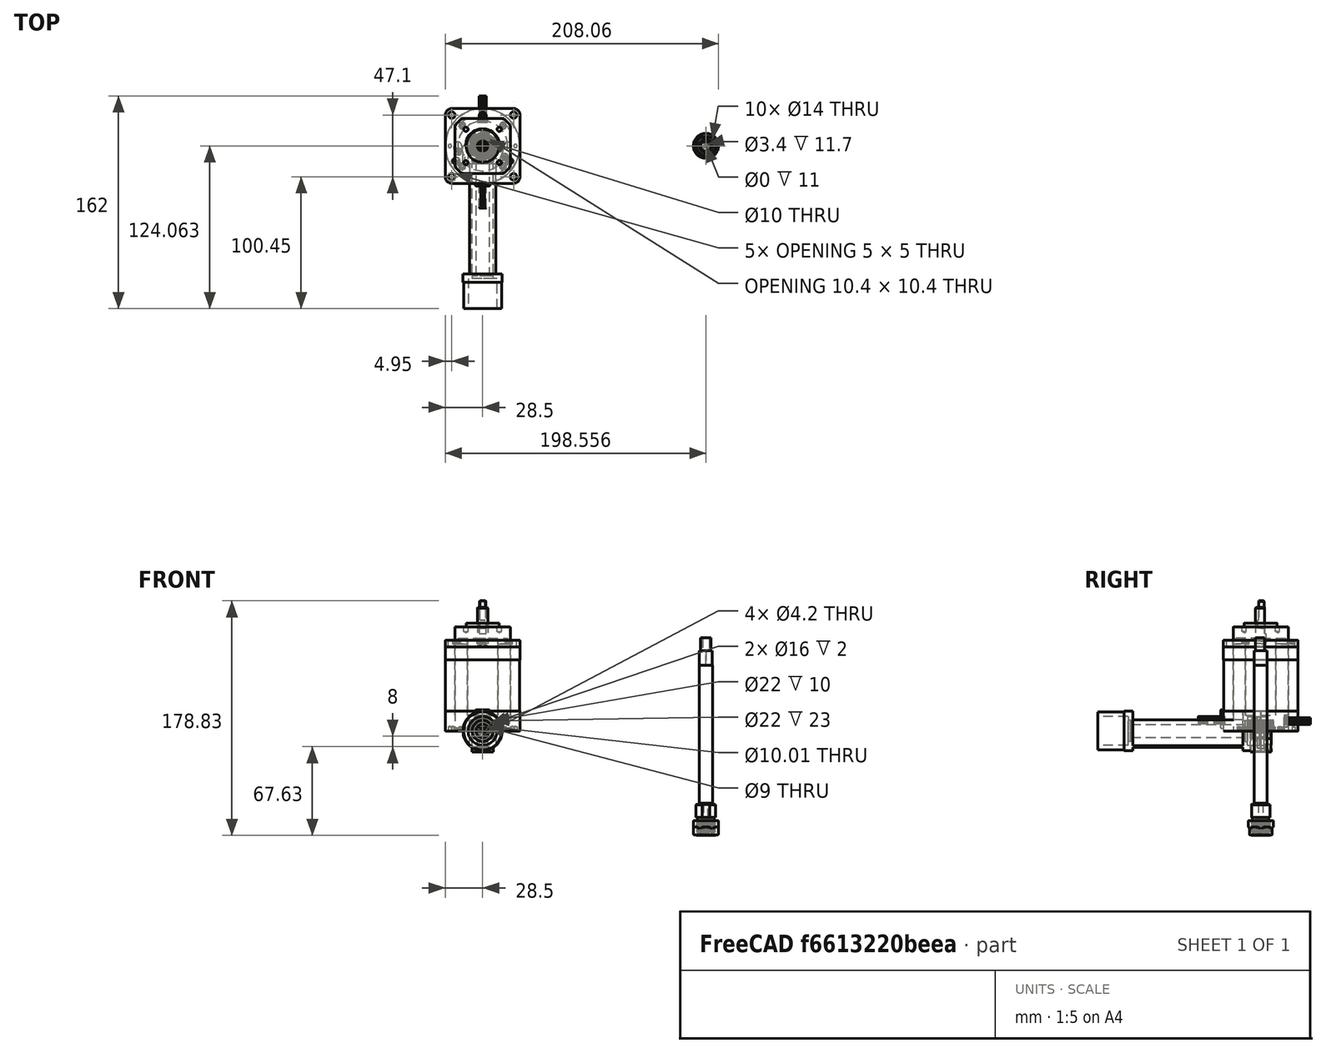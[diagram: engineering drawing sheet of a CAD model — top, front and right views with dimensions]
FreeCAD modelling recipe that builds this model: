
FCSTD DOCUMENT  (FreeCAD 0.21R31155 (Git))
Label: ToolPostDrill
License: All rights reserved
LicenseURL: http://en.wikipedia.org/wiki/All_rights_reserved
objects: TechDraw::DrawViewDimension×42, Sketcher::SketchObject×33, PartDesign::CoordinateSystem×27, PartDesign::Pocket×25, App::Link×18, App::Part×14, PartDesign::Pad×11, PartDesign::Body×10, TechDraw::DrawViewPart×7, Part::Feature×5, PartDesign::Chamfer×5, App::DocumentObjectGroup×4, PartDesign::FeaturePython×4, TechDraw::DrawSVGTemplate×3, TechDraw::DrawPage×3, TechDraw::DrawViewSection×2, PartDesign::ShapeBinder×2, Spreadsheet::Sheet×1, App::FeaturePython×1, PartDesign::Revolution×1
note: 165 computed .brp shape members not serialized (recipe doc carries the construction recipe); baked Part::Feature solids carry a one-line shape summary decoded from their .brp
EXTERNAL_REF file=BLDC Adapter.FCStd obj=MotorFlange
EXTERNAL_REF file=BLDC Adapter.FCStd obj=Part006
EXTERNAL_REF file=BLDC Adapter.FCStd obj=MountingFlange
EXTERNAL_REF file=ToolPost.FCStd obj=Part
EXTERNAL_REF file=ToolPost.FCStd obj=ToolBackRight
EXTERNAL_REF file=ConnectorHousing.FCStd obj=Part
EXTERNAL_REF file=ConnectorHousing.FCStd obj=Back

FEATURE [Spreadsheet::Sheet] Spreadsheet
  Configuration = 2
  cells = A4=Part; B4=HousingDiameter; C4=Length; D4=ToolHeight; E4=ToolHolderHeigth; F4=ShaftPosition; G4=ToolPostLength; H4=ColletShaftBoring; I4=BearingDiameter; J4=BearingWidth; K4=BearingDiameterBase; L4=BearingInnerDiameter; M4=BearingInnerPocketDepth; N4=ShaftDiameter; O4=LockNutThickness; P4=LockNutWasherThickness; Q4=LockNutBoltDiameter; R4=LockNutBoltThreadDiameter; S4=ShaftThreadDiameter; T4=ShaftEndDiameter; U4=ShaftEndLength; V4=ShaftEndDpocketLength; W4=MotorShaftDlength; X4=Wallthickness; Y4=MountingShaftDiameter; Z4=MountingShaftLength; AA4=FrontSpacerWidth; AB4=GearLengthSpindle; AC4=GearHeight; AD4=GearModule; AE4=GearTeeth; AF4=GearHelix; AG4=GearLengthBLDC; AH4=GearShaftPocketDepth; AI4=GearLockBoltThreadDiameter; AJ4=GearLockBoltThreadSeparation; AK4=GearLockBoltPosition; A5==hiddenref(.Configuration.String); B5(HousingDiameter)==.B8; C5(Length)==.C8; D5(ToolHeight)==.D8; E5(ToolHolderHeigth)==.E8; F5(ShaftPosition)==.F8; G5(ToolPostLength)==.G8; H5(ColletShaftBoring)==.H8; I5(BearingDiameter)==.I8; J5(BearingWidth)==.J8; K5(BearingDiameterBase)==.K8; L5(BearingInnerDiameter)==.L8; M5(BearingInnerPocketDepth)==.M8; N5(ShaftDiameter)==.N8; O5(LockNutThickness)==.O8; P5(LockNutWasherThickness)==.P8; Q5(LockNutBoltDiameter)==.Q8; R5(LockNutBoltThreadDiameter)==.R8; S5(ShaftThreadDiameter)==.S8; T5(ShaftEndDiameter)==.T8; U5(ShaftEndLength)==.U8; V5(ShaftEndDpocketLength)==.V8; W5(MotorShaftDlength)==.W8; X5(Wallthickness)==.X8; Y5(MountingShaftDiameter)==.Y8; Z5(MountingShaftLength)==.Z8; AA5(FrontSpacerWidth)==.AA8; AB5(GearLengthSpindle)==.AB8; AC5(GearHeight)==.AC8; AD5(GearModule)==.AD8; AE5(GearTeeth)==.AE8; AF5(GearHelix)==.AF8; AG5(GearLengthBLDC)==.AG8; AH5(GearShaftPocketDepth)==.AH8; AI5(GearLockBoltThreadDiameter)==.AI8; AJ5(GearLockBoltSeparation)==.AJ8; AK5(GearLockBoltPosition)==.AK8; AL5(GearShaftOuterDiameter)==.AL8; A6=BF290 Houder Vertical; B6=29.9; C6=150; D6=12.5; E6=21; F6=10; G6=80; H6=10; I6=22; J6=6; K6=14; L6=18; M6=2; N6=10; O6=5; P6=3; Q6=3; R6=2.5; S6=9.800000000000001; T6=8; U6=10; V6=10; W6=20; X6=3; Y6=28.9; Z6=20; AA6=4; AB6=14; AC6=6; AD6=1.5; AE6=12; AF6=0; AG6=26; AH6=11; AI6=4.2; AJ6=8; AK6=6; AL6=18; A7=DC300 Houder; B7=29.9; C7=150; D7=8.25; E7=14; F7=10; G7=50; H7=10; I7=22; J7=6; K7=14; L7=18; M7=2; N7=10; O7=15; P7=3; Q7=3; R7=2.5; S7=9.800000000000001; T7=8; U7=23; V7=10; W7=17; X7=3; Y7=26; Z7=12; AA7=4; AB7=12; AC7=8; AD7=1.5; AE7=12; AF7=0; AG7=26; AH7=10; AI7=4.2; AJ7=6; AK7=4; AL7=16; A8=BF290 Houder Horizontal; B8=29.9; C8=150; D8=12.5; E8=21; F8=10; G8=80; H8=10; I8=22; J8=6; K8=14; L8=18; M8=2; N8=10; O8=5; P8=3; Q8=3; R8=2.5; S8=9.800000000000001; T8=8; U8=10; V8=10; W8=20; X8=3; Y8=28.9; Z8=20; AA8=4; AB8=14; AC8=8; AD8=1; AE8=18; AF8=0; AG8=24; AH8=11; AI8=4.2; AJ8=8; AK8=4; AL8=16; A12=CalculatedFields; A13=FrontBearingPocketDepth; B13(FrontBearingPocketDepth)==BearingWidth + FrontSpacerWidth; C13=10; A14=BackBearingPocketDepth; B14(BackBearingPocketDepth)==MountingShaftLength + Wallthickness; C14=23; A15=BearingInnerPocketDiameter; B15(BearingInnerPocketDiameter)==(BearingDiameterBase + BearingInnerDiameter) / 2; A16=HousingLength; B16(HousingLength)==FrontBearingPocketDepth + Wallthickness + ToolPostPocketLength + Wallthickness + BackBearingPocketDepth + 1; +40 more cells
  expr: .Configuration.Enum = cells[<<A6:|>>]
  expr: .cells.Bind.B5.ZZ5 = tuple(.cells; <<B>> + str(hiddenref(Configuration) + 6); <<ZZ>> + str(hiddenref(Configuration) + 6))
FEATURE [Sketcher::SketchObject] Sketch
  FullyConstrained = true
  MapMode = 5
  Placement = pos=(0,0,0) rot=(1,0,0;1.5708rad)
  Support = -> [XZ_Plane005]
  expr: Constraints[1] = Spreadsheet.HousingDiameter
  sketch-geometry (1):
    g0: Circle CenterX=0 CenterY=0 CenterZ=0 NormalX=0 NormalY=0 NormalZ=1 AngleXU=0 Radius=14.95
  constraints (2):
    c: Coincident(g0,g-1)
    c: Diameter(g0) = 29.9
FEATURE [PartDesign::Pad] Pad001  label="Housing001"
  Direction = (0,-1,-2e-16)
  Length = 124
  Length2 = 10
  Placement = pos=(0,0,0) rot=(1,0,0;1.5708rad)
  Profile = -> Sketch
  ReferenceAxis = -> Sketch [N_Axis]
  Type = 0
  expr: Length = Spreadsheet.HousingLength
FEATURE [Sketcher::SketchObject] Sketch001
  FullyConstrained = true
  MapMode = 5
  Placement = pos=(0,0,0) rot=(-1,0,0;1.5708rad)
  Support = -> [Pad001]
  expr: Constraints[1] = Spreadsheet.BearingDiameter
  sketch-geometry (1):
    g0: Circle CenterX=0 CenterY=0 CenterZ=0 NormalX=0 NormalY=0 NormalZ=1 AngleXU=0 Radius=11
  constraints (2):
    c: Coincident(g0,g-1)
    c: Diameter(g0) = 22
FEATURE [PartDesign::Pocket] Pocket  label="FrontBearingPocket"
  BaseFeature = -> Pad001
  Direction = (0,-1,-2e-16)
  Length = 10
  Length2 = 5
  Placement = pos=(0,0,0) rot=(1,0,0;1.5708rad)
  Profile = -> Sketch001
  ReferenceAxis = -> Sketch001 [N_Axis]
  Type = 0
  expr: Length = Spreadsheet.FrontBearingPocketDepth
FEATURE [Sketcher::SketchObject] Sketch002
  FullyConstrained = true
  MapMode = 5
  Placement = pos=(0,-10,0) rot=(-1,0,0;1.5708rad)
  Support = -> [Pocket]
  expr: Constraints[1] = Spreadsheet.ShaftBoringDiameter
  sketch-geometry (1):
    g0: Circle CenterX=0 CenterY=0 CenterZ=0 NormalX=0 NormalY=0 NormalZ=1 AngleXU=0 Radius=5.005
  constraints (2):
    c: Coincident(g0,g-1)
    c: Diameter(g0) = 10.01
FEATURE [Sketcher::SketchObject] Sketch004
  AttachmentOffset = pos=(0,0,13.5) rot=(0,0,1;0rad)
  FullyConstrained = true
  MapMode = 5
  Placement = pos=(0,-13.5,-3e-15) rot=(1,0,0;1.5708rad)
  Support = -> [XZ_Plane005]
  expr: .AttachmentOffset.Base.z = Spreadsheet.ToolPostPocketPositionH
  expr: Constraints[13] = Spreadsheet.HousingDiameter + 1
  expr: Constraints[2] = Spreadsheet.ToolHeight
  expr: Constraints[3] = Spreadsheet.HousingDiameter + 1
  expr: Constraints[5] = Spreadsheet.ToolHolderHeigth
  expr: Constraints[7] = Spreadsheet.ShaftPosition
  sketch-geometry (13):
    g0: LineSegment StartX=-9.29289 StartY=-12.5 StartZ=0 EndX=9.29289 EndY=-12.5 EndZ=0
    g1: LineSegment StartX=15.45 StartY=-15.45 StartZ=0 EndX=-15.45 EndY=-15.45 EndZ=0
    g2: LineSegment StartX=-10 StartY=8.5 StartZ=0 EndX=10 EndY=8.5 EndZ=0
    g3: LineSegment StartX=-10 StartY=-11.7929 StartZ=0 EndX=-10 EndY=8.5 EndZ=0
    g4: LineSegment StartX=10 StartY=8.5 StartZ=0 EndX=10 EndY=-11.7929 EndZ=0
    g5: LineSegment StartX=-15.45 StartY=-15.45 StartZ=0 EndX=-15.45 EndY=15.45 EndZ=0
    g6: LineSegment StartX=-15.45 StartY=15.45 StartZ=0 EndX=15.45 EndY=15.45 EndZ=0
    g7: LineSegment StartX=15.45 StartY=15.45 StartZ=0 EndX=15.45 EndY=-15.45 EndZ=0
    g8: GeomPoint X=-15.45 Y=15.45 Z=0
    g9: GeomPoint X=-10 Y=8.5 Z=0
    g10: GeomPoint X=10 Y=8.5 Z=0
    g11: LineSegment StartX=-10 StartY=-11.7929 StartZ=0 EndX=-9.29289 EndY=-12.5 EndZ=0
    g12: LineSegment StartX=10 StartY=-11.7929 StartZ=0 EndX=9.29289 EndY=-12.5 EndZ=0
  constraints (33):
    c: Horizontal(g0)
    c: Symmetric(g1,g1,g-2)
    c: DistanceY(g0,g-1) = 12.5
    c: DistanceX(g1,g1) = 30.9
    c: Symmetric(g9,g10,g-2)
    c: DistanceY(g0,g10) = 21
    c: Vertical(g3)
    c: DistanceX(g-1,g10) = 10
    c: Coincident(g1,g5)
    c: Vertical(g5)
    c: Horizontal(g6)
    c: Coincident(g6,g7)
    c: Coincident(g7,g1)
    c: DistanceY(g7,g7) = 30.9
    c: PointOnObject(g8,g6)
    c: PointOnObject(g8,g5)
    c: Symmetric(g6,g1,g-1)
    c: PointOnObject(g9,g2)
    c: PointOnObject(g9,g3)
    c: PointOnObject(g10,g2)
    c: PointOnObject(g10,g4)
    c: Vertical(g4)
    c: Coincident(g3,g2)
    c: Coincident(g4,g2)
    c: Coincident(g5,g6)
    c: Coincident(g4,g12)
    c: Coincident(g12,g0)
    c: Angle(g12,g0) = 2.35619
    c: Coincident(g3,g11)
    c: Coincident(g11,g0)
    c: Angle(g0,g11) = 2.35619
    c: Distance(g11) = 1
    c: Equal(g11,g12)
FEATURE [Part::Feature] Part__Feature003  label="Body"
  shape: bbox 22 x 6 x 22 mm, 52 faces (baked)
FEATURE [PartDesign::CoordinateSystem] LCS_1  label="Inner"
  AttacherType = Attacher::AttachEngine3D
  MapMode = 11
  Placement = pos=(0,-3,-9e-16) rot=(0.57735,-0.57735,0.57735;2.0944rad)
  Support = -> [Part__Feature003]
FEATURE [PartDesign::CoordinateSystem] LCS_Origin
  AttacherType = Attacher::AttachEngine3D
  MapMode = 2
  Support = -> [X_Axis007]
FEATURE [App::DocumentObjectGroup] Constraints
FEATURE [App::FeaturePython] Variables  # WARN: FeaturePython — macro-defined, semantics opaque (R4)
  Type = App::PropertyContainer
FEATURE [App::DocumentObjectGroup] Configurations
FEATURE [App::Link] Housing  label="Housing002"
  AssemblyType = Part::Link
  AttachedBy = #FrontBearing
  AttachedTo = Parent Assembly#LCS_Origin
  AttachmentOffset = pos=(0,0,72) rot=(0.57735,-0.57735,-0.57735;4.18879rad)
  LinkPlacement = pos=(2.2e-15,10,72) rot=(0,0,1;0rad)
  LinkedObject = -> Part001
  Placement = pos=(2.2e-15,10,72) rot=(0,0,1;0rad)
  SolverId = Asm4EE
  expr: Placement = LCS_Origin.Placement * AttachmentOffset * FrontBearing.Placement ^ -1
FEATURE [App::Link] Bearing002
  AssemblyType = Part::Link
  AttachedBy = #LCS_1
  AttachedTo = Housing#FrontBearing
  AttachmentOffset = pos=(0,0,0) rot=(0,-1,0;3.14159rad)
  LinkPlacement = pos=(1.3e-15,3,72) rot=(0,0,1;0rad)
  LinkedObject = -> Bearing001
  Placement = pos=(1.3e-15,3,72) rot=(0,0,1;0rad)
  SolverId = Asm4EE
  expr: Placement = Housing.Placement * FrontBearing.Placement * AttachmentOffset * LCS_1.Placement ^ -1
FEATURE [App::Link] Bearing003
  AssemblyType = Part::Link
  AttachedBy = #LCS_1
  AttachedTo = Housing#BackBearing
  AttachmentOffset = pos=(0,0,0) rot=(1,0,0;3.14159rad)
  LinkPlacement = pos=(-1.47e-14,-94,72) rot=(0,0,-1;3.14159rad)
  LinkedObject = -> Bearing001
  Placement = pos=(-1.47e-14,-94,72) rot=(0,0,-1;3.14159rad)
  SolverId = Asm4EE
  expr: Placement = Housing.Placement * BackBearing.Placement * AttachmentOffset * LCS_1.Placement ^ -1
FEATURE [PartDesign::CoordinateSystem] Outer
  AttacherType = Attacher::AttachEngine3D
  MapMode = 11
  Placement = pos=(0,3,9e-16) rot=(0.57735,-0.57735,0.57735;2.0944rad)
  Support = -> [Part__Feature003]
FEATURE [App::Part] Bearing001  label="Bearing"
  Group = -> [Part__Feature003,LCS_1,Outer]
  Origin = -> Origin006
FEATURE [Part::Feature] Part__Feature004  label="ER11A_Mutter_Komponente1_einzeln v2"
  Placement = pos=(170.057,0.0630184,-68.3269) rot=(0,1,0;3.14159rad)
  shape: bbox 20.48 x 19.46 x 11.62 mm, 87 faces (baked)
FEATURE [Part::Feature] Part__Feature005  label="Kopf_Aufnahme"
  shape: bbox 15.02 x 14.53 x 22.42 mm, 56 faces (baked)
FEATURE [Sketcher::SketchObject] Sketch011
  FullyConstrained = true
  MapMode = 11
  Placement = pos=(170,-2.2e-15,-55) rot=(0,0,1;1.5708rad)
  Support = -> [Part__Feature005]
  expr: Constraints[1] = Spreadsheet.ShaftDiameter
  sketch-geometry (1):
    g0: Circle CenterX=0 CenterY=0 CenterZ=0 NormalX=0 NormalY=0 NormalZ=1 AngleXU=0 Radius=5
  constraints (2):
    c: Coincident(g0,g-1)
    c: Diameter(g0) = 10
FEATURE [PartDesign::Pad] Pad  label="Shaft"
  Direction = (0,0,1)
  Length = 105
  Length2 = 10
  Profile = -> Sketch011
  ReferenceAxis = -> Sketch011 [N_Axis]
  Type = 0
  expr: Length = Spreadsheet.ShaftLength
FEATURE [Sketcher::SketchObject] Sketch012
  FullyConstrained = false
  MapMode = 11
  Placement = pos=(170,-1.8e-15,50) rot=(0,0,1;3.14159rad)
  Support = -> [Pad]
  expr: Constraints[2] = Spreadsheet.ShaftThreadDiameter
  sketch-geometry (2):
    g0: Circle CenterX=-3.1e-05 CenterY=0 CenterZ=0 NormalX=0 NormalY=0 NormalZ=1 AngleXU=0 Radius=0.00074
    g1: Circle CenterX=-3.1e-05 CenterY=0 CenterZ=0 NormalX=0 NormalY=0 NormalZ=1 AngleXU=0 Radius=4.9
  constraints (3):
    c: PointOnObject(g0,g-1)
    c: Coincident(g1,g0)
    c: Diameter(g1) = 9.8
FEATURE [PartDesign::Pad] Pad004  label="ShaftThread"
  BaseFeature = -> Pad
  Direction = (0,0,1)
  Length = 11
  Length2 = 10
  Profile = -> Sketch012
  ReferenceAxis = -> Sketch012 [N_Axis]
  Type = 0
  expr: Length = Spreadsheet.ShaftThreadLength
FEATURE [Sketcher::SketchObject] Sketch013
  FullyConstrained = true
  MapMode = 11
  Placement = pos=(170,-2e-15,61) rot=(0,0,-1;1.5708rad)
  Support = -> [Pad004]
  expr: Constraints[1] = Spreadsheet.ShaftEndDiameter
  sketch-geometry (1):
    g0: Circle CenterX=0 CenterY=0 CenterZ=0 NormalX=0 NormalY=0 NormalZ=1 AngleXU=0 Radius=4
  constraints (2):
    c: Coincident(g0,g-1)
    c: Diameter(g0) = 8
FEATURE [PartDesign::Pad] Pad005  label="ShaftEnd"
  BaseFeature = -> Pad004
  Direction = (0,0,1)
  Length = 10
  Length2 = 10
  Profile = -> Sketch013
  ReferenceAxis = -> Sketch013 [N_Axis]
  Type = 0
  expr: Length = Spreadsheet.ShaftEndLength
FEATURE [PartDesign::CoordinateSystem] SpindelFrontBearing
  AttacherType = Attacher::AttachEngine3D
  AttachmentOffset = pos=(0,0,-1) rot=(0,0,1;0rad)
  MapMode = 11
  Placement = pos=(170,-2e-15,-56) rot=(0,0,1;3.14159rad)
FEATURE [App::Link] Spindle  label="Spindle001"
  AssemblyType = Part::Link
  AttachedBy = #SpindelFrontBearing
  AttachedTo = SpacerFront#Back002
  AttachmentOffset = pos=(0,0,0) rot=(0,0,-1;3.14159rad)
  LinkPlacement = pos=(2.7e-14,-46,242) rot=(-0.57735,-0.57735,0.57735;4.18879rad)
  LinkedObject = -> Part003
  Placement = pos=(2.7e-14,-46,242) rot=(-0.57735,-0.57735,0.57735;4.18879rad)
  SolverId = Asm4EE
  expr: Placement = SpacerFront.Placement * Back002.Placement * AttachmentOffset * SpindelFrontBearing.Placement ^ -1
FEATURE [Part::Feature] Part__Feature  label="57BLR70-24-02"
  shape: bbox 61.7 x 78.35 x 94.1 mm, 300 faces, 2 solids (baked)
FEATURE [PartDesign::CoordinateSystem] Flange
  AttacherType = Attacher::AttachEngine3D
  MapMode = 11
  Placement = pos=(0,-1.2e-15,69.1) rot=(0,0,-1;1.5708rad)
  Support = -> [Part__Feature]
FEATURE [PartDesign::CoordinateSystem] ShaftTop
  AttacherType = Attacher::AttachEngine3D
  MapMode = 5
  Placement = pos=(0,0,94.1) rot=(0,0,1;0rad)
  Support = -> [Part__Feature]
FEATURE [App::Link] BLDCmotor  label="BLDCmotor001"
  AssemblyType = Part::Link
  AttachedBy = #Flange
  AttachedTo = BLDC_adapter#MotorFlange
  AttachmentOffset = pos=(0,0,0) rot=(1,0,0;3.14159rad)
  LinkPlacement = pos=(-3.42e-14,-209.1,90) rot=(-1,0,0;1.5708rad)
  LinkedObject = -> Part005
  Placement = pos=(-3.42e-14,-209.1,90) rot=(-1,0,0;1.5708rad)
  SolverId = Asm4EE
  expr: Placement = BLDC_adapter.Placement * BLDC_Adapter#MotorFlange.Placement * AttachmentOffset * Flange.Placement ^ -1
FEATURE [Sketcher::SketchObject] Sketch017
  FullyConstrained = true
  MapMode = 5
  Support = -> [XY_Plane019]
  expr: Constraints[2] = Spreadsheet.ShaftDiameter
  expr: Constraints[3] = Spreadsheet.SpacerOuterDiameter
  sketch-geometry (2):
    g0: Circle CenterX=0 CenterY=0 CenterZ=0 NormalX=0 NormalY=0 NormalZ=1 AngleXU=0 Radius=5
    g1: Circle CenterX=0 CenterY=0 CenterZ=0 NormalX=0 NormalY=0 NormalZ=1 AngleXU=0 Radius=10.95
  constraints (4):
    c: Coincident(g0,g-1)
    c: Coincident(g1,g0)
    c: Diameter(g0) = 10
    c: Diameter(g1) = 21.9
FEATURE [PartDesign::Pad] Pad007
  Direction = (0,0,1)
  Length = 4
  Length2 = 10
  Profile = -> Sketch017
  ReferenceAxis = -> Sketch017 [N_Axis]
  Type = 0
  expr: Length = Spreadsheet.FrontSpacerWidth
FEATURE [PartDesign::Chamfer] Chamfer
  Angle = 45
  Base = -> Pad007 [Face4,Face3]
  BaseFeature = -> Pad007
  ChamferType = 0
  FlipDirection = false
  Size = 0.25
  Size2 = 1
  SupportTransform = false
  UseAllEdges = false
FEATURE [PartDesign::CoordinateSystem] Front002
  AttacherType = Attacher::AttachEngine3D
  MapMode = 11
  Placement = pos=(0,0,4) rot=(0,0,1;1.5708rad)
  Support = -> [Chamfer]
FEATURE [PartDesign::CoordinateSystem] Back002
  AttacherType = Attacher::AttachEngine3D
  MapMode = 11
  Placement = pos=(0,0,0) rot=(0,0,1;1.5708rad)
  Support = -> [Chamfer]
FEATURE [App::Link] SpacerFront  label="SpacerFront001"
  AssemblyType = Part::Link
  AttachedBy = #Front002
  AttachedTo = Bearing002#Outer
  AttachmentOffset = pos=(0,0,0) rot=(0,0,-1;3.14159rad)
  LinkPlacement = pos=(3.7e-15,10,72) rot=(0,0.707107,-0.707107;3.14159rad)
  LinkedObject = -> Part006
  Placement = pos=(3.7e-15,10,72) rot=(0,0.707107,-0.707107;3.14159rad)
  SolverId = Asm4EE
  expr: Placement = Bearing002.Placement * Outer.Placement * AttachmentOffset * Front002.Placement ^ -1
FEATURE [App::Link] LockNut001
  AssemblyType = Part::Link
  AttachedBy = #Front003
  AttachedTo = Bearing003#Outer
  AttachmentOffset = pos=(0,0,0) rot=(0,0,-1;3.14159rad)
  LinkPlacement = pos=(-1.42e-14,-102,72) rot=(0,-1,0;4.71239rad)
  LinkedObject = -> LockNut
  Placement = pos=(-1.42e-14,-102,72) rot=(0,-1,0;4.71239rad)
  SolverId = Asm4EE
  expr: Placement = Bearing003.Placement * Outer.Placement * AttachmentOffset * Front003.Placement ^ -1
FEATURE [Sketcher::SketchObject] Sketch019
  FullyConstrained = false
  MapMode = 5
  Placement = pos=(0,0,71) rot=(0,0,1;0rad)
  Support = -> [Pad005]
  expr: Constraints[10] = Spreadsheet.ShaftEndDiameter + 1
  expr: Constraints[9] = Spreadsheet.ShaftDPocketPosition
  sketch-geometry (5):
    g0: LineSegment StartX=165.948 StartY=5 StartZ=0 EndX=174.948 EndY=5 EndZ=0
    g1: LineSegment StartX=174.948 StartY=5 StartZ=0 EndX=174.948 EndY=3 EndZ=0
    g2: LineSegment StartX=174.948 StartY=3 StartZ=0 EndX=165.948 EndY=3 EndZ=0
    g3: LineSegment StartX=165.948 StartY=3 StartZ=0 EndX=165.948 EndY=5 EndZ=0
    g4: GeomPoint X=170.529 Y=0 Z=0
  constraints (12):
    c: Coincident(g0,g1)
    c: Coincident(g1,g2)
    c: Coincident(g2,g3)
    c: Coincident(g3,g0)
    c: Horizontal(g0)
    c: Horizontal(g2)
    c: Vertical(g1)
    c: Vertical(g3)
    c: PointOnObject(g4,g-1)
    c: DistanceY(g4,g1) = 3
    c: DistanceX(g0,g0) = 9
    c: DistanceY(g1,g1) = 2
FEATURE [PartDesign::Pocket] Pocket006
  BaseFeature = -> Pad005
  Direction = (0,0,-1)
  Length = 10
  Length2 = 5
  Profile = -> Sketch019
  ReferenceAxis = -> Sketch019 [N_Axis]
  Type = 0
  expr: Length = Spreadsheet.ShaftEndDpocketLength
FEATURE [PartDesign::Body] Body  label="Body004"
  Group = -> [Sketch011,Pad,Sketch012,Pad004,Sketch013,Pad005,Sketch019,Pocket006]
  Origin = -> Origin014
  Tip = -> Pocket006
FEATURE [PartDesign::CoordinateSystem] Back004
  AttacherType = Attacher::AttachEngine3D
  MapMode = 11
  Placement = pos=(170,-1.8e-15,71) rot=(0,0,1;0rad)
  Support = -> [Pocket006]
FEATURE [TechDraw::DrawSVGTemplate] Template
  EditableTexts = Designed_by_Name=Huub Buis; Drawing_number=Drawing number; FC-Date=20221216; FC-SC=Scale; FC-SH=Sheet; FC-Title=BF290 Drill holder - ER11; Subtitle=V01; Weight=Weight
  Height = 210
  Orientation = 1
  Template = C:/Program Files/FreeCAD 0.19/data/Mod/TechDraw/Templates/A4_LandscapeTD.svg
  Width = 297
FEATURE [Sketcher::SketchObject] Sketch021
  FullyConstrained = true
  MapMode = 5
  Placement = pos=(0,-10,0) rot=(-1,0,0;1.5708rad)
  Support = -> [Pocket]
  expr: Constraints[1] = Spreadsheet.BearingInnerPocketDiameter
  sketch-geometry (1):
    g0: Circle CenterX=0 CenterY=0 CenterZ=0 NormalX=0 NormalY=0 NormalZ=1 AngleXU=0 Radius=8
  constraints (2):
    c: Coincident(g0,g-1)
    c: Diameter(g0) = 16
FEATURE [PartDesign::Pocket] Pocket007  label="FrontBearingInnerPocket"
  BaseFeature = -> Pocket
  Direction = (0,-1,-2e-16)
  Length = 2
  Length2 = 5
  Placement = pos=(0,0,0) rot=(1,0,0;1.5708rad)
  Profile = -> Sketch021
  ReferenceAxis = -> Sketch021 [N_Axis]
  Type = 0
  expr: Length = Spreadsheet.BearingInnerPocketDepth
FEATURE [PartDesign::Pocket] Pocket001  label="ShaftPocket"
  BaseFeature = -> Pocket007
  Direction = (0,-1,-2e-16)
  Length = 5
  Length2 = 5
  Placement = pos=(0,0,0) rot=(1,0,0;1.5708rad)
  Profile = -> Sketch002
  ReferenceAxis = -> Sketch002 [N_Axis]
  Type = 1
FEATURE [Sketcher::SketchObject] Sketch003
  FullyConstrained = true
  MapMode = 5
  Placement = pos=(0,-124,3e-16) rot=(1,0,0;1.5708rad)
  Support = -> [Pocket001]
  expr: Constraints[1] = Spreadsheet.BearingDiameter
  sketch-geometry (1):
    g0: Circle CenterX=0 CenterY=0 CenterZ=0 NormalX=0 NormalY=0 NormalZ=1 AngleXU=0 Radius=11
  constraints (2):
    c: Coincident(g0,g-1)
    c: Diameter(g0) = 22
FEATURE [PartDesign::Pocket] Pocket002  label="BackBearingPocket"
  BaseFeature = -> Pocket001
  Direction = (0,1,2e-16)
  Length = 23
  Length2 = 5
  Placement = pos=(0,0,0) rot=(1,0,0;1.5708rad)
  Profile = -> Sketch003
  ReferenceAxis = -> Sketch003 [N_Axis]
  Type = 0
  expr: Length = Spreadsheet.BackBearingPocketDepth
FEATURE [Sketcher::SketchObject] Sketch022
  FullyConstrained = true
  MapMode = 5
  Placement = pos=(0,-101,2.24e-14) rot=(1,0,0;1.5708rad)
  Support = -> [Pocket002]
  expr: Constraints[1] = Spreadsheet.BearingInnerPocketDiameter
  sketch-geometry (1):
    g0: Circle CenterX=0 CenterY=0 CenterZ=0 NormalX=0 NormalY=0 NormalZ=1 AngleXU=0 Radius=8
  constraints (2):
    c: Coincident(g0,g-1)
    c: Diameter(g0) = 16
FEATURE [PartDesign::Pocket] Pocket008  label="BackBearingInnerPocket"
  BaseFeature = -> Pocket002
  Direction = (0,1,-2e-16)
  Length = 2
  Length2 = 5
  Placement = pos=(0,0,0) rot=(1,0,0;1.5708rad)
  Profile = -> Sketch022
  ReferenceAxis = -> Sketch022 [N_Axis]
  Type = 0
  expr: Length = Spreadsheet.BearingInnerPocketDepth
FEATURE [PartDesign::Pocket] Pocket003  label="ToolPostPocket"
  BaseFeature = -> Pocket008
  Direction = (0,1,2e-16)
  Length = 84
  Length2 = 5
  Placement = pos=(0,0,0) rot=(1,0,0;1.5708rad)
  Profile = -> Sketch004
  ReferenceAxis = -> Sketch004 [N_Axis]
  Reversed = true
  Type = 0
  expr: Length = Spreadsheet.ToolPostPocketLength
FEATURE [PartDesign::CoordinateSystem] BackBearing
  AttacherType = Attacher::AttachEngine3D
  MapMode = 11
  Placement = pos=(0,-101,-5.6e-15) rot=(0.57735,-0.57735,0.57735;2.0944rad)
  Support = -> [Pocket003]
FEATURE [PartDesign::CoordinateSystem] FrontBearing
  AttacherType = Attacher::AttachEngine3D
  MapMode = 11
  Placement = pos=(0,-10,2.2e-15) rot=(0.57735,-0.57735,-0.57735;4.18879rad)
  Support = -> [Pocket003]
FEATURE [Sketcher::SketchObject] Sketch015
  FullyConstrained = true
  MapMode = 5
  Placement = pos=(0,-124,3e-16) rot=(1,0,0;1.5708rad)
  Support = -> [Pocket003]
  expr: Constraints[1] = Spreadsheet.MountingShaftDiameter
  expr: Constraints[3] = Spreadsheet.HousingDiameter + 1
  sketch-geometry (2):
    g0: Circle CenterX=0 CenterY=0 CenterZ=0 NormalX=0 NormalY=0 NormalZ=1 AngleXU=0 Radius=14.45
    g1: Circle CenterX=0 CenterY=0 CenterZ=0 NormalX=0 NormalY=0 NormalZ=1 AngleXU=0 Radius=15.45
  constraints (4):
    c: Coincident(g0,g-1)
    c: Diameter(g0) = 28.9
    c: Coincident(g1,g0)
    c: Diameter(g1) = 30.9
FEATURE [PartDesign::Pocket] Pocket005  label="MountingShaftPocket"
  BaseFeature = -> Pocket003
  Direction = (0,1,2e-16)
  Length = 20
  Length2 = 5
  Placement = pos=(0,0,0) rot=(1,0,0;1.5708rad)
  Profile = -> Sketch015
  ReferenceAxis = -> Sketch015 [N_Axis]
  Type = 0
  expr: Length = Spreadsheet.MountingShaftLength
FEATURE [PartDesign::Body] Body001  label="HousingBody"
  Group = -> [Sketch,Pad001,Sketch001,Pocket,Pocket007,Sketch002,Pocket001,Sketch003,Pocket002,Pocket008,Sketch004,Pocket003,Sketch015,Pocket005,Sketch021,Sketch022]
  Origin = -> Origin005
  Tip = -> Pocket005
FEATURE [PartDesign::CoordinateSystem] MountingShaft001  label="MountingShaft002"
  AttacherType = Attacher::AttachEngine3D
  MapMode = 11
  Placement = pos=(0,-124,-5e-16) rot=(0.57735,-0.57735,0.57735;2.0944rad)
  Support = -> [Pocket005]
FEATURE [App::Part] Part001  label="Housing"
  Group = -> [Body001,BackBearing,FrontBearing,MountingShaft001]
  Origin = -> Origin004
FEATURE [TechDraw::DrawViewPart] View  label="Housing003"
  CoarseView = false
  Direction = (1,0,0)
  Focus = 100
  HardHidden = true
  IsoCount = 0
  IsoHidden = false
  IsoVisible = false
  LockPosition = false
  Perspective = false
  Rotation = 0
  ScaleType = 0
  SeamHidden = false
  SeamVisible = false
  SmoothHidden = false
  SmoothVisible = true
  Source = -> [Part001]
  X = 89.0384
  XDirection = (0,1,0)
  Y = 160.956
FEATURE [TechDraw::DrawViewSection] SectionView  label="Section A - A"
  BaseView = -> View
  CoarseView = false
  CutSurfaceDisplay = 2
  Direction = (0,1e-16,-1)
  FileGeomPattern = C:/Program Files/FreeCAD 0.19/data/Mod/TechDraw/PAT/FCPAT.pat
  FileHatchPattern = C:/Program Files/FreeCAD 0.19/data/Mod/TechDraw/Patterns/simple.svg
  Focus = 100
  FuseBeforeCut = false
  HardHidden = false
  HatchScale = 1
  IsoCount = 0
  IsoHidden = false
  IsoVisible = false
  LockPosition = false
  NameGeomPattern = Diamant
  Perspective = false
  Rotation = 0
  ScaleType = 0
  SeamHidden = false
  SeamVisible = true
  SectionDirection = 4
  SectionNormal = (0,1e-16,-1)
  SectionOrigin = (0,-61.99,0.033)
  SectionSymbol = A
  SmoothHidden = false
  SmoothVisible = true
  Source = -> [Part001]
  TrimAfterCut = false
  X = 135.319
  XDirection = (0,1,1e-16)
  Y = 101.209
FEATURE [TechDraw::DrawViewDimension] Dimension010
  AngleOverride = false
  Arbitrary = false
  ArbitraryTolerances = false
  EqualTolerance = true
  ExtensionAngle = 0
  FormatSpec = %.2f
  FormatSpecOverTolerance = %+.2f
  FormatSpecUnderTolerance = %+.2f
  Inverted = false
  LineAngle = 0
  LockPosition = false
  MeasureType = 1
  OverTolerance = 0
  References2D = -> [SectionView]
  Rotation = 0
  ScaleType = 0
  TheoreticalExact = false
  Type = 1
  UnderTolerance = 0
  X = -55.4134
  Y = -34.9784
FEATURE [TechDraw::DrawSVGTemplate] Template001
  EditableTexts = Designed_by_Name=Designed by Name; Drawing_number=Drawing number; FC-Date=Date; FC-SC=Scale; FC-SH=Sheet; FC-Title=Title; Subtitle=Subtitle; Weight=Weight
  Height = 210
  Orientation = 1
  Template = C:/Program Files/FreeCAD 0.19/data/Mod/TechDraw/Templates/A4_LandscapeTD.svg
  Width = 297
FEATURE [Sketcher::SketchObject] Sketch023
  FullyConstrained = true
  MapMode = 5
  Placement = pos=(0,0,4) rot=(0,0,1;0rad)
  Support = -> [Pad007]
  expr: Constraints[2] = Spreadsheet.BearingInnerPocketDiameter
  expr: Constraints[3] = Spreadsheet.SpacerOuterDiameter
  sketch-geometry (2):
    g0: Circle CenterX=0 CenterY=0 CenterZ=0 NormalX=0 NormalY=0 NormalZ=1 AngleXU=0 Radius=8
    g1: Circle CenterX=0 CenterY=0 CenterZ=0 NormalX=0 NormalY=0 NormalZ=1 AngleXU=0 Radius=10.95
  constraints (4):
    c: Coincident(g0,g-1)
    c: Coincident(g1,g0)
    c: Diameter(g0) = 16
    c: Diameter(g1) = 21.9
FEATURE [PartDesign::Pocket] Pocket009
  BaseFeature = -> Chamfer
  Direction = (0,0,-1)
  Length = 1
  Length2 = 5
  Profile = -> Sketch023
  ReferenceAxis = -> Sketch023 [N_Axis]
  Type = 0
FEATURE [PartDesign::Body] Body005  label="Body006"
  Group = -> [Sketch017,Pad007,Chamfer,Sketch023,Pocket009]
  Origin = -> Origin019
  Tip = -> Pocket009
FEATURE [App::Part] Part006  label="SpacerFront"
  Group = -> [Body005,Front002,Back002]
  Origin = -> Origin018
FEATURE [TechDraw::DrawViewPart] View004  label="Spacer FV"
  CoarseView = false
  Direction = (0,-1,0)
  Focus = 100
  HardHidden = false
  IsoCount = 0
  IsoHidden = false
  IsoVisible = false
  LockPosition = false
  Perspective = false
  Rotation = 0
  ScaleType = 0
  SeamHidden = false
  SeamVisible = true
  SmoothHidden = false
  SmoothVisible = true
  Source = -> [Part006]
  X = 32.6631
  XDirection = (1,0,0)
  Y = 163.585
FEATURE [TechDraw::DrawViewDimension] Dimension016
  AngleOverride = false
  Arbitrary = false
  ArbitraryTolerances = false
  EqualTolerance = true
  ExtensionAngle = 0
  FormatSpec = %.2f
  FormatSpecOverTolerance = %+.2f
  FormatSpecUnderTolerance = %+.2f
  Inverted = false
  LineAngle = 0
  LockPosition = false
  MeasureType = 1
  OverTolerance = 0
  References2D = -> [View004]
  Rotation = 0
  ScaleType = 0
  TheoreticalExact = false
  Type = 2
  UnderTolerance = 0
  X = 18.1775
  Y = 27.7079
FEATURE [TechDraw::DrawViewDimension] Dimension017
  AngleOverride = false
  Arbitrary = false
  ArbitraryTolerances = false
  EqualTolerance = true
  ExtensionAngle = 0
  FormatSpec = %.2f
  FormatSpecOverTolerance = %+.2f
  FormatSpecUnderTolerance = %+.2f
  Inverted = false
  LineAngle = 0
  LockPosition = false
  MeasureType = 1
  OverTolerance = 0
  References2D = -> [View004]
  Rotation = 0
  ScaleType = 0
  TheoreticalExact = false
  Type = 2
  UnderTolerance = 0
  X = 27.9886
  Y = 28.1012
FEATURE [TechDraw::DrawViewSection] SectionView001  label="Section A - A001"
  BaseView = -> View004
  CoarseView = false
  CutSurfaceDisplay = 2
  Direction = (1,0,0)
  FileGeomPattern = C:/Program Files/FreeCAD 0.19/data/Mod/TechDraw/PAT/FCPAT.pat
  FileHatchPattern = C:/Program Files/FreeCAD 0.19/data/Mod/TechDraw/Patterns/simple.svg
  Focus = 100
  FuseBeforeCut = false
  HardHidden = false
  HatchScale = 1
  IsoCount = 0
  IsoHidden = false
  IsoVisible = false
  LockPosition = false
  NameGeomPattern = Diamant
  Perspective = false
  Rotation = 0
  ScaleType = 0
  SeamHidden = false
  SeamVisible = true
  SectionDirection = 4
  SectionNormal = (1,0,0)
  SectionOrigin = (0.02,0,2)
  SectionSymbol = A
  SmoothHidden = false
  SmoothVisible = true
  Source = -> [Part006]
  TrimAfterCut = false
  X = 104.982
  XDirection = (0,0,1)
  Y = 166.774
FEATURE [TechDraw::DrawViewDimension] Dimension021
  AngleOverride = false
  Arbitrary = false
  ArbitraryTolerances = false
  EqualTolerance = true
  ExtensionAngle = 0
  FormatSpec = %.2f
  FormatSpecOverTolerance = %+.2f
  FormatSpecUnderTolerance = %+.2f
  Inverted = false
  LineAngle = 0
  LockPosition = false
  MeasureType = 1
  OverTolerance = 0
  References2D = -> [SectionView001]
  Rotation = 0
  ScaleType = 0
  TheoreticalExact = false
  Type = 2
  UnderTolerance = 0
  X = 9.95315
  Y = 1.13586
FEATURE [TechDraw::DrawViewDimension] Dimension022
  AngleOverride = false
  Arbitrary = false
  ArbitraryTolerances = false
  EqualTolerance = true
  ExtensionAngle = 0
  FormatSpec = %.2f
  FormatSpecOverTolerance = %+.2f
  FormatSpecUnderTolerance = %+.2f
  Inverted = false
  LineAngle = 0
  LockPosition = false
  MeasureType = 1
  OverTolerance = 0
  References2D = -> [SectionView001]
  Rotation = 0
  ScaleType = 0
  TheoreticalExact = false
  Type = 2
  UnderTolerance = 0
  X = 17.7375
  Y = 1.77002
FEATURE [TechDraw::DrawViewDimension] Dimension023
  AngleOverride = false
  Arbitrary = false
  ArbitraryTolerances = false
  EqualTolerance = true
  ExtensionAngle = 0
  FormatSpec = %.2f
  FormatSpecOverTolerance = %+.2f
  FormatSpecUnderTolerance = %+.2f
  Inverted = false
  LineAngle = 0
  LockPosition = false
  MeasureType = 1
  OverTolerance = 0
  References2D = -> [SectionView001]
  Rotation = 0
  ScaleType = 0
  TheoreticalExact = false
  Type = 2
  UnderTolerance = 0
  X = 26.9666
  Y = 2.34357
FEATURE [TechDraw::DrawViewDimension] Dimension024
  AngleOverride = false
  Arbitrary = false
  ArbitraryTolerances = false
  EqualTolerance = true
  ExtensionAngle = 0
  FormatSpec = %.2f
  FormatSpecOverTolerance = %+.2f
  FormatSpecUnderTolerance = %+.2f
  Inverted = false
  LineAngle = 0
  LockPosition = false
  MeasureType = 1
  OverTolerance = 0
  References2D = -> [SectionView]
  Rotation = 0
  ScaleType = 0
  TheoreticalExact = false
  Type = 2
  UnderTolerance = 0
  X = -70.9878
  Y = 2.35719
FEATURE [TechDraw::DrawViewDimension] Dimension025
  AngleOverride = false
  Arbitrary = false
  ArbitraryTolerances = false
  EqualTolerance = true
  ExtensionAngle = 0
  FormatSpec = %.2f
  FormatSpecOverTolerance = %+.2f
  FormatSpecUnderTolerance = %+.2f
  Inverted = false
  LineAngle = 0
  LockPosition = false
  MeasureType = 1
  OverTolerance = 0
  References2D = -> [SectionView]
  Rotation = 0
  ScaleType = 0
  TheoreticalExact = false
  Type = 2
  UnderTolerance = 0
  X = -86.2687
  Y = 2.07158
FEATURE [TechDraw::DrawViewDimension] Dimension026
  AngleOverride = false
  Arbitrary = false
  ArbitraryTolerances = false
  EqualTolerance = true
  ExtensionAngle = 0
  FormatSpec = %.2f
  FormatSpecOverTolerance = %+.2f
  FormatSpecUnderTolerance = %+.2f
  Inverted = false
  LineAngle = 0
  LockPosition = false
  MeasureType = 1
  OverTolerance = 0
  References2D = -> [SectionView]
  Rotation = 0
  ScaleType = 0
  TheoreticalExact = false
  Type = 2
  UnderTolerance = 0
  X = -97.273
  Y = 3.64245
FEATURE [TechDraw::DrawViewDimension] Dimension027
  AngleOverride = false
  Arbitrary = false
  ArbitraryTolerances = false
  EqualTolerance = true
  ExtensionAngle = 0
  FormatSpec = %.2f
  FormatSpecOverTolerance = %+.2f
  FormatSpecUnderTolerance = %+.2f
  Inverted = false
  LineAngle = 0
  LockPosition = false
  MeasureType = 1
  OverTolerance = 0
  References2D = -> [SectionView]
  Rotation = 0
  ScaleType = 0
  TheoreticalExact = false
  Type = 2
  UnderTolerance = 0
  X = -105.127
  Y = 3.78525
FEATURE [TechDraw::DrawViewDimension] Dimension029
  AngleOverride = false
  Arbitrary = false
  ArbitraryTolerances = false
  EqualTolerance = true
  ExtensionAngle = 0
  FormatSpec = %.2f
  FormatSpecOverTolerance = %+.2f
  FormatSpecUnderTolerance = %+.2f
  Inverted = false
  LineAngle = 0
  LockPosition = false
  MeasureType = 1
  OverTolerance = 0
  References2D = -> [SectionView]
  Rotation = 0
  ScaleType = 0
  TheoreticalExact = false
  Type = 1
  UnderTolerance = 0
  X = 81.9719
  Y = 3.92927
FEATURE [TechDraw::DrawViewDimension] Dimension032
  AngleOverride = false
  Arbitrary = false
  ArbitraryTolerances = false
  EqualTolerance = true
  ExtensionAngle = 0
  FormatSpec = %.2f
  FormatSpecOverTolerance = %+.2f
  FormatSpecUnderTolerance = %+.2f
  Inverted = false
  LineAngle = 0
  LockPosition = false
  MeasureType = 1
  OverTolerance = 0
  References2D = -> [SectionView]
  Rotation = 0
  ScaleType = 0
  TheoreticalExact = false
  Type = 1
  UnderTolerance = 0
  X = 81.9308
  Y = 13.2358
FEATURE [TechDraw::DrawSVGTemplate] Template002
  EditableTexts = Designed_by_Name=Designed by Name; Drawing_number=Drawing number; FC-Date=Date; FC-SC=Scale; FC-SH=Sheet; FC-Title=Title; Subtitle=Subtitle; Weight=Weight
  Height = 210
  Orientation = 1
  Template = C:/Program Files/FreeCAD 0.19/data/Mod/TechDraw/Templates/A4_LandscapeTD.svg
  Width = 297
FEATURE [Sketcher::SketchObject] Sketch024
  FullyConstrained = true
  MapMode = 5
  Placement = pos=(0,0,0) rot=(0.57735,0.57735,0.57735;2.0944rad)
  Support = -> [YZ_Plane025]
  expr: Constraints[13] = Spreadsheet.LockNutThreadDiameter / 2
  expr: Constraints[14] = Spreadsheet.LockNutDiameter / 2
  expr: Constraints[15] = Spreadsheet.BearingDiameterBase / 2
  expr: Constraints[17] = Spreadsheet.LockNutThickness
  sketch-geometry (6):
    g0: LineSegment StartX=0 StartY=10.9 StartZ=0 EndX=4.5 EndY=10.9 EndZ=0
    g1: LineSegment StartX=4.5 StartY=10.9 StartZ=0 EndX=4.5 EndY=7 EndZ=0
    g2: LineSegment StartX=4.5 StartY=7 StartZ=0 EndX=5 EndY=7 EndZ=0
    g3: LineSegment StartX=5 StartY=7 StartZ=0 EndX=5 EndY=4.5 EndZ=0
    g4: LineSegment StartX=5 StartY=4.5 StartZ=0 EndX=0 EndY=4.5 EndZ=0
    g5: LineSegment StartX=0 StartY=4.5 StartZ=0 EndX=0 EndY=10.9 EndZ=0
  constraints (18):
    c: PointOnObject(g0,g-2)
    c: Horizontal(g0)
    c: Coincident(g0,g1)
    c: Vertical(g1)
    c: Coincident(g1,g2)
    c: Horizontal(g2)
    c: Coincident(g2,g3)
    c: Vertical(g3)
    c: Coincident(g3,g4)
    c: PointOnObject(g4,g-2)
    c: Horizontal(g4)
    c: Coincident(g4,g5)
    c: Coincident(g5,g0)
    c: DistanceY(g-1,g4) = 4.5
    c: DistanceY(g-1,g0) = 10.9
    c: DistanceY(g-1,g2) = 7
    c: DistanceX(g2,g2) = 0.5
    c: DistanceX(g4,g4) = 5
FEATURE [PartDesign::Revolution] Revolution
  Angle = 360
  Axis = (1e-16,1,-1e-16)
  Base = (0,0,0)
  Placement = pos=(0,0,0) rot=(0.57735,0.57735,0.57735;2.0944rad)
  Profile = -> Sketch024
  ReferenceAxis = -> Y_Axis025
FEATURE [Sketcher::SketchObject] Sketch025
  FullyConstrained = true
  MapMode = 5
  Placement = pos=(0,-5e-16,0) rot=(0.57735,0.57735,-0.57735;2.0944rad)
  Support = -> [Revolution]
  expr: Constraints[2] = Spreadsheet.LockNutBoltSeparation
  expr: Constraints[3] = Spreadsheet.LockNutBoltDiameter
  sketch-geometry (2):
    g0: Circle CenterX=0 CenterY=8 CenterZ=0 NormalX=0 NormalY=0 NormalZ=1 AngleXU=0 Radius=1.5
    g1: Circle CenterX=0 CenterY=-8 CenterZ=0 NormalX=0 NormalY=0 NormalZ=1 AngleXU=0 Radius=1.5
  constraints (5):
    c: PointOnObject(g0,g-2)
    c: Symmetric(g0,g1,g-1)
    c: DistanceY(g1,g0) = 16
    c: Diameter(g0) = 3
    c: Equal(g0,g1)
FEATURE [PartDesign::Pocket] Pocket010
  BaseFeature = -> Revolution
  Direction = (2e-16,1,-4e-16)
  Length = 5
  Length2 = 5
  Placement = pos=(0,0,0) rot=(0.57735,0.57735,0.57735;2.0944rad)
  Profile = -> Sketch025
  ReferenceAxis = -> Sketch025 [N_Axis]
  Type = 1
FEATURE [PartDesign::Body] Body007  label="LockNutNut"
  Group = -> [Sketch024,Revolution,Sketch025,Pocket010]
  Origin = -> Origin025
  Tip = -> Pocket010
FEATURE [Sketcher::SketchObject] Sketch026
  FullyConstrained = true
  MapMode = 5
  Placement = pos=(0,0,0) rot=(1,0,0;1.5708rad)
  Support = -> [XZ_Plane026]
  expr: Constraints[2] = Spreadsheet.LockNutThreadDiameter
  expr: Constraints[3] = Spreadsheet.LockNutBoltThreadDiameter
  expr: Constraints[5] = Spreadsheet.LockNutDiameter
  expr: Constraints[7] = Spreadsheet.LockNutBoltSeparation
  sketch-geometry (4):
    g0: Circle CenterX=0 CenterY=0 CenterZ=0 NormalX=0 NormalY=0 NormalZ=1 AngleXU=0 Radius=4.5
    g1: Circle CenterX=0 CenterY=0 CenterZ=0 NormalX=0 NormalY=0 NormalZ=1 AngleXU=0 Radius=10.9
    g2: Circle CenterX=-8 CenterY=0 CenterZ=0 NormalX=0 NormalY=0 NormalZ=1 AngleXU=0 Radius=1.25
    g3: Circle CenterX=8 CenterY=0 CenterZ=0 NormalX=0 NormalY=0 NormalZ=1 AngleXU=0 Radius=1.25
  constraints (9):
    c: Coincident(g0,g-1)
    c: Coincident(g1,g0)
    c: Diameter(g0) = 9
    c: Diameter(g2) = 2.5
    c: Equal(g2,g3)
    c: Diameter(g1) = 21.8
    c: Symmetric(g3,g2,g0)
    c: Distance(g2,g3) = 16
    c: PointOnObject(g2,g-1)
FEATURE [PartDesign::Pad] Pad009
  Direction = (0,-1,-2e-16)
  Length = 3
  Length2 = 10
  Placement = pos=(0,0,0) rot=(1,0,0;1.5708rad)
  Profile = -> Sketch026
  ReferenceAxis = -> Sketch026 [N_Axis]
  Type = 0
  expr: Length = Spreadsheet.LockNutWasherThickness
FEATURE [PartDesign::CoordinateSystem] Back
  AttacherType = Attacher::AttachEngine3D
  MapMode = 11
  Placement = pos=(0,-3,7e-16) rot=(0.57735,-0.57735,0.57735;2.0944rad)
  Support = -> [Pad009]
FEATURE [PartDesign::Body] Body008  label="LockNutDisk"
  Group = -> [Sketch026,Pad009,Back]
  Origin = -> Origin026
  Placement = pos=(0,-1,0) rot=(0,0,1;0rad)
  Tip = -> Pad009
FEATURE [PartDesign::CoordinateSystem] Front003
  AttacherType = Attacher::AttachEngine3D
  MapMode = 11
  Placement = pos=(6e-16,5,-1.8e-15) rot=(-1,0,0;1.5708rad)
  Support = -> [Pocket010]
FEATURE [App::Part] LockNut
  Group = -> [Body007,Body008,Front003]
  Origin = -> Origin022
FEATURE [PartDesign::CoordinateSystem] ThreadStart
  AttacherType = Attacher::AttachEngine3D
  MapMode = 11
  Placement = pos=(170,-1.8e-15,50) rot=(0,0,1;3.14159rad)
  Support = -> [Pocket006]
FEATURE [PartDesign::CoordinateSystem] EndStart
  AttacherType = Attacher::AttachEngine3D
  MapMode = 11
  Placement = pos=(170,-2e-15,61) rot=(0,0,-1;1.5708rad)
  Support = -> [Pocket006]
FEATURE [App::Part] ER11_Spindle_8x100mm_v2  label="ER11 Spindle_8x100mm v2"
  Group = -> [Part__Feature004,Part__Feature005,Body,EndStart]
  Origin = -> Origin
FEATURE [App::Part] Part003  label="Spindle"
  Group = -> [ER11_Spindle_8x100mm_v2,SpindelFrontBearing,Back004,ThreadStart]
  Origin = -> Origin013
FEATURE [TechDraw::DrawViewPart] View006  label="Part"
  CoarseView = false
  Direction = (0.851,0.429,0.303)
  Focus = 100
  HardHidden = false
  IsoCount = 0
  IsoHidden = false
  IsoVisible = false
  LockPosition = false
  Perspective = false
  Rotation = 0
  ScaleType = 0
  SeamHidden = false
  SeamVisible = true
  SmoothHidden = false
  SmoothVisible = true
  Source = -> [Part003]
  X = 211.81
  XDirection = (-0.45,0.295,0.843)
  Y = 155.608
FEATURE [TechDraw::DrawViewPart] View007  label="FV"
  CoarseView = false
  Direction = (1,0,0)
  Focus = 100
  HardHidden = false
  IsoCount = 0
  IsoHidden = false
  IsoVisible = false
  LockPosition = false
  Perspective = false
  Rotation = 270
  ScaleType = 0
  SeamHidden = false
  SeamVisible = true
  SmoothHidden = false
  SmoothVisible = true
  Source = -> [Part003]
  X = 84.063
  XDirection = (0,1,0)
  Y = 81.1692
FEATURE [TechDraw::DrawViewDimension] Dimension036
  AngleOverride = false
  Arbitrary = false
  ArbitraryTolerances = false
  EqualTolerance = true
  ExtensionAngle = 0
  FormatSpec = %.2f
  FormatSpecOverTolerance = %+.2f
  FormatSpecUnderTolerance = %+.2f
  Inverted = false
  LineAngle = 0
  LockPosition = false
  MeasureType = 1
  OverTolerance = 0
  References2D = -> [View007]
  Rotation = 0
  ScaleType = 0
  TheoreticalExact = false
  Type = 1
  UnderTolerance = 0
  X = 89.3849
  Y = 22.8891
FEATURE [TechDraw::DrawViewDimension] Dimension039
  AngleOverride = false
  Arbitrary = true
  ArbitraryTolerances = false
  EqualTolerance = true
  ExtensionAngle = 0
  FormatSpec = M10x1
  FormatSpecOverTolerance = %+.2f
  FormatSpecUnderTolerance = %+.2f
  Inverted = false
  LineAngle = 0
  LockPosition = false
  MeasureType = 1
  OverTolerance = 0
  References2D = -> [View007]
  Rotation = 0
  ScaleType = 0
  TheoreticalExact = false
  Type = 2
  UnderTolerance = 0
  X = 84.0724
  Y = -7.58136
FEATURE [TechDraw::DrawViewDimension] Dimension035
  AngleOverride = false
  Arbitrary = false
  ArbitraryTolerances = false
  EqualTolerance = true
  ExtensionAngle = 0
  FormatSpec = %.2f
  FormatSpecOverTolerance = %+.2f
  FormatSpecUnderTolerance = %+.2f
  Inverted = false
  LineAngle = 0
  LockPosition = false
  MeasureType = 1
  OverTolerance = 0
  References2D = -> [View007]
  Rotation = 0
  ScaleType = 0
  TheoreticalExact = false
  Type = 1
  UnderTolerance = 0
  X = 43.1486
  Y = 22.9128
FEATURE [TechDraw::DrawViewDimension] Dimension034
  AngleOverride = false
  Arbitrary = false
  ArbitraryTolerances = false
  EqualTolerance = true
  ExtensionAngle = 0
  FormatSpec = %.2f
  FormatSpecOverTolerance = %+.2f
  FormatSpecUnderTolerance = %+.2f
  Inverted = false
  LineAngle = 0
  LockPosition = false
  MeasureType = 1
  OverTolerance = 0
  References2D = -> [View007]
  Rotation = 0
  ScaleType = 0
  TheoreticalExact = false
  Type = 1
  UnderTolerance = 0
  X = 2.07988
  Y = 18.9234
FEATURE [TechDraw::DrawViewDimension] Dimension038
  AngleOverride = false
  Arbitrary = true
  ArbitraryTolerances = false
  EqualTolerance = true
  ExtensionAngle = 0
  FormatSpec = 8 mm D=7
  FormatSpecOverTolerance = %+.2f
  FormatSpecUnderTolerance = %+.2f
  Inverted = false
  LineAngle = 0
  LockPosition = false
  MeasureType = 1
  OverTolerance = 0
  References2D = -> [View007]
  Rotation = 0
  ScaleType = 0
  TheoreticalExact = false
  Type = 2
  UnderTolerance = 0
  X = 107.08
  Y = 1.78744
FEATURE [TechDraw::DrawViewDimension] Dimension050
  AngleOverride = false
  Arbitrary = false
  ArbitraryTolerances = false
  EqualTolerance = true
  ExtensionAngle = 0
  FormatSpec = %.2f
  FormatSpecOverTolerance = %+.2f
  FormatSpecUnderTolerance = %+.2f
  Inverted = false
  LineAngle = 0
  LockPosition = false
  MeasureType = 1
  OverTolerance = 0
  References2D = -> [View007]
  Rotation = 0
  ScaleType = 0
  TheoreticalExact = false
  Type = 1
  UnderTolerance = 0
  X = 5.62656
  Y = -22.4269
FEATURE [TechDraw::DrawPage] Page002  label="Spindle002"
  KeepUpdated = true
  NextBalloonIndex = 1
  ProjectionType = 0
  Template = -> Template002
  Views = -> [View006,View007,Dimension034,Dimension035,Dimension036,Dimension038,Dimension039,Dimension050]
FEATURE [App::Link] Link  label="BLDC adapter"
  LinkedObject = -> <external BLDC Adapter.FCStd>#Part006
FEATURE [App::Link] BLDC_adapter  label="BLDC adapter001"
  AssemblyType = Part::Link
  AttachedBy = #MountingFlange
  AttachedTo = Housing#BackBearing
  AttachmentOffset = pos=(0,0,6) rot=(0,0,1;0rad)
  LinkPlacement = pos=(-2.69e-14,-136,90) rot=(-1,0,0;4.71239rad)
  LinkedObject = -> <external BLDC Adapter.FCStd>#Part006
  Placement = pos=(-2.69e-14,-136,90) rot=(-1,0,0;4.71239rad)
  SolverId = Asm4EE
  expr: Placement = Housing.Placement * BackBearing.Placement * AttachmentOffset * BLDC_Adapter#MountingFlange.Placement ^ -1
FEATURE [TechDraw::DrawViewDimension] Dimension051
  AngleOverride = false
  Arbitrary = false
  ArbitraryTolerances = false
  EqualTolerance = true
  ExtensionAngle = 0
  FormatSpec = %.2f
  FormatSpecOverTolerance = %+.2f
  FormatSpecUnderTolerance = %+.2f
  Inverted = false
  LineAngle = 0
  LockPosition = false
  MeasureType = 1
  OverTolerance = 0
  References2D = -> [SectionView]
  Rotation = 0
  ScaleType = 0
  TheoreticalExact = false
  Type = 1
  UnderTolerance = 0
  X = -49.9996
  Y = -20.3399
FEATURE [TechDraw::DrawViewDimension] Dimension052
  AngleOverride = false
  Arbitrary = false
  ArbitraryTolerances = false
  EqualTolerance = true
  ExtensionAngle = 0
  FormatSpec = %.2f
  FormatSpecOverTolerance = %+.2f
  FormatSpecUnderTolerance = %+.2f
  Inverted = false
  LineAngle = 0
  LockPosition = false
  MeasureType = 1
  OverTolerance = 0
  References2D = -> [SectionView]
  Rotation = 0
  ScaleType = 0
  TheoreticalExact = false
  Type = 1
  UnderTolerance = 0
  X = 58.3662
  Y = -30.6408
FEATURE [TechDraw::DrawViewDimension] Dimension053
  AngleOverride = false
  Arbitrary = false
  ArbitraryTolerances = false
  EqualTolerance = true
  ExtensionAngle = 0
  FormatSpec = %.2f
  FormatSpecOverTolerance = %+.2f
  FormatSpecUnderTolerance = %+.2f
  Inverted = false
  LineAngle = 0
  LockPosition = false
  MeasureType = 1
  OverTolerance = 0
  References2D = -> [View]
  Rotation = 0
  ScaleType = 0
  TheoreticalExact = false
  Type = 2
  UnderTolerance = 0
  X = -10.9965
  Y = 2.46336
FEATURE [TechDraw::DrawViewDimension] Dimension054
  AngleOverride = false
  Arbitrary = false
  ArbitraryTolerances = false
  EqualTolerance = true
  ExtensionAngle = 0
  FormatSpec = %.2f
  FormatSpecOverTolerance = %+.2f
  FormatSpecUnderTolerance = %+.2f
  Inverted = false
  LineAngle = 0
  LockPosition = false
  MeasureType = 1
  OverTolerance = 0
  References2D = -> [View]
  Rotation = 0
  ScaleType = 0
  TheoreticalExact = false
  Type = 2
  UnderTolerance = 0
  X = -27.025
  Y = -0.912105
FEATURE [TechDraw::DrawViewDimension] Dimension055
  AngleOverride = false
  Arbitrary = false
  ArbitraryTolerances = false
  EqualTolerance = true
  ExtensionAngle = 0
  FormatSpec = %.2f
  FormatSpecOverTolerance = %+.2f
  FormatSpecUnderTolerance = %+.2f
  Inverted = false
  LineAngle = 0
  LockPosition = false
  MeasureType = 1
  OverTolerance = 0
  References2D = -> [View]
  Rotation = 0
  ScaleType = 0
  TheoreticalExact = false
  Type = 2
  UnderTolerance = 0
  X = 35.803
  Y = 20.2875
FEATURE [TechDraw::DrawViewDimension] Dimension056
  AngleOverride = false
  Arbitrary = false
  ArbitraryTolerances = false
  EqualTolerance = true
  ExtensionAngle = 0
  FormatSpec = %.2f
  FormatSpecOverTolerance = %+.2f
  FormatSpecUnderTolerance = %+.2f
  Inverted = false
  LineAngle = 0
  LockPosition = false
  MeasureType = 1
  OverTolerance = 0
  References2D = -> [View]
  Rotation = 0
  ScaleType = 0
  TheoreticalExact = false
  Type = 2
  UnderTolerance = 0
  X = 10.413
  Y = 2.27836
FEATURE [TechDraw::DrawViewPart] View010  label="FV001"
  CoarseView = false
  Direction = (0,1,0)
  Focus = 100
  HardHidden = true
  IsoCount = 0
  IsoHidden = false
  IsoVisible = false
  LockPosition = false
  Perspective = false
  Rotation = 0
  ScaleType = 0
  SeamHidden = false
  SeamVisible = true
  SmoothHidden = false
  SmoothVisible = true
  Source = -> [Part001]
  X = 208.178
  XDirection = (-1,0,0)
  Y = 162.049
FEATURE [TechDraw::DrawViewDimension] Dimension059
  AngleOverride = false
  Arbitrary = false
  ArbitraryTolerances = false
  EqualTolerance = true
  ExtensionAngle = 0
  FormatSpec = %.2f
  FormatSpecOverTolerance = %+.2f
  FormatSpecUnderTolerance = %+.2f
  Inverted = false
  LineAngle = 0
  LockPosition = false
  MeasureType = 1
  OverTolerance = 0
  References2D = -> [SectionView]
  Rotation = 0
  ScaleType = 0
  TheoreticalExact = false
  Type = 2
  UnderTolerance = 0
  X = 33.7046
  Y = 18.1312
FEATURE [TechDraw::DrawViewDimension] Dimension060
  AngleOverride = false
  Arbitrary = false
  ArbitraryTolerances = false
  EqualTolerance = true
  ExtensionAngle = 0
  FormatSpec = %.2f
  FormatSpecOverTolerance = %+.2f
  FormatSpecUnderTolerance = %+.2f
  Inverted = false
  LineAngle = 0
  LockPosition = false
  MeasureType = 1
  OverTolerance = 0
  References2D = -> [SectionView]
  Rotation = 0
  ScaleType = 0
  TheoreticalExact = false
  Type = 2
  UnderTolerance = 0
  X = 33.6277
  Y = -15.1838
FEATURE [TechDraw::DrawViewDimension] Dimension061
  AngleOverride = false
  Arbitrary = false
  ArbitraryTolerances = false
  EqualTolerance = true
  ExtensionAngle = 0
  FormatSpec = %.2f
  FormatSpecOverTolerance = %+.2f
  FormatSpecUnderTolerance = %+.2f
  Inverted = false
  LineAngle = 0
  LockPosition = false
  MeasureType = 1
  OverTolerance = 0
  References2D = -> [SectionView]
  Rotation = 0
  ScaleType = 0
  TheoreticalExact = false
  Type = 2
  UnderTolerance = 0
  X = -117.234
  Y = 4.08804
FEATURE [TechDraw::DrawViewDimension] Dimension062
  AngleOverride = false
  Arbitrary = false
  ArbitraryTolerances = false
  EqualTolerance = true
  ExtensionAngle = 0
  FormatSpec = %.2f
  FormatSpecOverTolerance = %+.2f
  FormatSpecUnderTolerance = %+.2f
  Inverted = false
  LineAngle = 0
  LockPosition = false
  MeasureType = 1
  OverTolerance = 0
  References2D = -> [SectionView]
  Rotation = 0
  ScaleType = 0
  TheoreticalExact = false
  Type = 1
  UnderTolerance = 0
  X = 6.3015
  Y = 23.8148
FEATURE [TechDraw::DrawViewDimension] Dimension063
  AngleOverride = false
  Arbitrary = false
  ArbitraryTolerances = false
  EqualTolerance = true
  ExtensionAngle = 0
  FormatSpec = %.2f
  FormatSpecOverTolerance = %+.2f
  FormatSpecUnderTolerance = %+.2f
  Inverted = false
  LineAngle = 0
  LockPosition = false
  MeasureType = 1
  OverTolerance = 0
  References2D = -> [View]
  Rotation = 0
  ScaleType = 0
  TheoreticalExact = false
  Type = 1
  UnderTolerance = 0
  X = -4.07398
  Y = 31.0599
FEATURE [TechDraw::DrawViewDimension] Dimension
  AngleOverride = false
  Arbitrary = false
  ArbitraryTolerances = false
  EqualTolerance = true
  ExtensionAngle = 0
  FormatSpec = %.2f
  FormatSpecOverTolerance = %+.2f
  FormatSpecUnderTolerance = %+.2f
  Inverted = false
  LineAngle = 0
  LockPosition = false
  MeasureType = 1
  OverTolerance = 0
  References2D = -> [View]
  Rotation = 0
  ScaleType = 0
  TheoreticalExact = false
  Type = 1
  UnderTolerance = 0
  X = -3.94092
  Y = 38.0271
FEATURE [TechDraw::DrawViewDimension] Dimension064
  AngleOverride = false
  Arbitrary = false
  ArbitraryTolerances = false
  EqualTolerance = true
  ExtensionAngle = 0
  FormatSpec = %.2f
  FormatSpecOverTolerance = %+.2f
  FormatSpecUnderTolerance = %+.2f
  Inverted = false
  LineAngle = 0
  LockPosition = false
  MeasureType = 1
  OverTolerance = 0
  References2D = -> [View]
  Rotation = 0
  ScaleType = 0
  TheoreticalExact = false
  Type = 1
  UnderTolerance = 0
  X = -48.4879
  Y = 23.5819
FEATURE [TechDraw::DrawViewDimension] Dimension065
  AngleOverride = false
  Arbitrary = false
  ArbitraryTolerances = false
  EqualTolerance = true
  ExtensionAngle = 0
  FormatSpec = %.2f
  FormatSpecOverTolerance = %+.2f
  FormatSpecUnderTolerance = %+.2f
  Inverted = false
  LineAngle = 0
  LockPosition = false
  MeasureType = 1
  OverTolerance = 0
  References2D = -> [View]
  Rotation = 0
  ScaleType = 0
  TheoreticalExact = false
  Type = 2
  UnderTolerance = 0
  X = 24.2358
  Y = 4.16273
FEATURE [TechDraw::DrawPage] Page  label="HousingDrawing"
  KeepUpdated = true
  NextBalloonIndex = 1
  ProjectionType = 0
  Template = -> Template
  Views = -> [View,SectionView,Dimension010,Dimension024,Dimension025,Dimension026,Dimension027,Dimension029,Dimension032,Dimension051,Dimension052,Dimension053,Dimension054,Dimension055,Dimension056,View010,Dimension059,Dimension060,Dimension061,Dimension062,Dimension063,Dimension,Dimension064,Dimension065]
FEATURE [Sketcher::SketchObject] Sketch031
  FullyConstrained = true
  MapMode = 5
  Support = -> [XY_Plane032]
  expr: Constraints[1] = Spreadsheet.GearShaftOuterDiameter
  sketch-geometry (1):
    g0: Circle CenterX=0 CenterY=0 CenterZ=0 NormalX=0 NormalY=0 NormalZ=1 AngleXU=0 Radius=8
  constraints (2):
    c: Coincident(g0,g-1)
    c: Diameter(g0) = 16
FEATURE [PartDesign::Pad] Pad012
  Direction = (0,0,1)
  Length = 6
  Length2 = 10
  Profile = -> Sketch031
  ReferenceAxis = -> Sketch031 [N_Axis]
  Reversed = true
  Type = 0
  expr: Length = Spreadsheet.GearLengthSpindle - Spreadsheet.GearHeight
FEATURE [Sketcher::SketchObject] Sketch032
  AttachmentOffset = pos=(0,0,-6) rot=(0,0,1;0rad)
  FullyConstrained = true
  MapMode = 5
  Placement = pos=(0,0,-6) rot=(0,0,1;0rad)
  Support = -> [XY_Plane032]
  expr: .AttachmentOffset.Base.z = -Spreadsheet.GearShaftLength
  expr: Constraints[4] = Spreadsheet.ShaftCouplerInnerDiameter
  expr: Constraints[5] = Spreadsheet.ShaftCouplerInnerDiameter / 2 - 1
  sketch-geometry (2):
    g0: ArcOfCircle CenterX=0 CenterY=0 CenterZ=0 NormalX=0 NormalY=0 NormalZ=1 AngleXU=0 Radius=4.075 StartAngle=2.28655 EndAngle=7.13823
    g1: LineSegment StartX=-2.67395 StartY=3.075 StartZ=0 EndX=2.67395 EndY=3.075 EndZ=0
  constraints (6):
    c: Coincident(g0,g-1)
    c: Horizontal(g1)
    c: Coincident(g0,g1)
    c: Coincident(g0,g1)
    c: Diameter(g0) = 8.15
    c: DistanceY(g0,g0) = 3.075
FEATURE [PartDesign::Pocket] Pocket011  label="ShaftPocket001"
  BaseFeature = -> Pad012
  Direction = (0,0,-1)
  Length = 11
  Length2 = 5
  Profile = -> Sketch032
  ReferenceAxis = -> Sketch032 [N_Axis]
  Reversed = true
  Type = 1
  expr: Length = Spreadsheet.GearShaftPocketDepth
FEATURE [App::Link] BevelGearSpindle  label="BevelGearSpindle001"
  AssemblyType = Part::Link
  AttachedBy = #Gear
  AttachedTo = Spindle#Back004
  LinkPlacement = pos=(-3.3e-14,-117,72) rot=(0,-0.707107,0.707107;3.14159rad)
  LinkedObject = -> Part009
  Placement = pos=(-3.3e-14,-117,72) rot=(0,-0.707107,0.707107;3.14159rad)
  SolverId = Asm4EE
  expr: Placement = Spindle.Placement * Back004.Placement * AttachmentOffset * Gear.Placement ^ -1
FEATURE [PartDesign::Chamfer] Chamfer002  label="Chamferhaft"
  Angle = 45
  Base = -> Pocket011 [Edge6,Edge7]
  BaseFeature = -> Pocket011
  ChamferType = 0
  FlipDirection = false
  Size = 0.3
  Size2 = 1
  SupportTransform = false
  UseAllEdges = false
FEATURE [PartDesign::FeaturePython] BevelGear002  # WARN: FeaturePython — macro-defined, semantics opaque (R4)
  AttacherType = Attacher::AttachEngine3D
  BaseFeature = -> Chamfer002
  angular_backlash = 0
  backlash = 0
  beta = 0
  clearance = 0.1
  dw = 18
  height = 8
  module = 1
  numpoints = 6
  pitch_angle = 45
  pressure_angle = 20
  reset_origin = true
  teeth = 18
  version = 0.0.4
  expr: angular_backlash = backlash / dw * 360° / pi
  expr: beta = Spreadsheet.GearHelix
  expr: dw = teeth * module
  expr: height = Spreadsheet.GearHeight
  expr: module = Spreadsheet.GearModule
  expr: teeth = Spreadsheet.GearTeeth
FEATURE [PartDesign::CoordinateSystem] Back005
  AttacherType = Attacher::AttachEngine3D
  MapMode = 11
  Placement = pos=(0,0,-6) rot=(0,0,1;1.5708rad)
  Support = -> [Chamfer002]
FEATURE [Sketcher::SketchObject] Sketch033
  FullyConstrained = true
  MapMode = 5
  Support = -> [XY_Plane034]
  expr: Constraints[1] = Spreadsheet.GearShaftOuterDiameter
  sketch-geometry (1):
    g0: Circle CenterX=0 CenterY=0 CenterZ=0 NormalX=0 NormalY=0 NormalZ=1 AngleXU=0 Radius=8
  constraints (2):
    c: Coincident(g0,g-1)
    c: Diameter(g0) = 16
FEATURE [PartDesign::Pad] Pad013
  Direction = (0,0,1)
  Length = 16
  Length2 = 10
  Profile = -> Sketch033
  ReferenceAxis = -> Sketch033 [N_Axis]
  Reversed = true
  Type = 0
  expr: Length = Spreadsheet.GearLengthBLDC - Spreadsheet.GearHeight
FEATURE [App::Link] BevelGearBLDC  label="BevelGearBLDC001"
  AssemblyType = Part::Link
  AttachedBy = #Gear003
  AttachedTo = BLDCmotor#ShaftTop
  AttachmentOffset = pos=(0,0,0) rot=(0,0,-1;3.14159rad)
  LinkPlacement = pos=(-2.68e-14,-115,90) rot=(0.57735,-0.57735,-0.57735;4.18879rad)
  LinkedObject = -> Part010
  Placement = pos=(-2.68e-14,-115,90) rot=(0.57735,-0.57735,-0.57735;4.18879rad)
  SolverId = Asm4EE
  expr: Placement = BLDCmotor.Placement * ShaftTop.Placement * AttachmentOffset * Gear003.Placement ^ -1
FEATURE [Sketcher::SketchObject] Sketch035
  FullyConstrained = true
  MapMode = 5
  Support = -> [XY_Plane032]
  expr: Constraints[1] = Spreadsheet.GearTeethPocketDiameter
  expr: Constraints[3] = Spreadsheet.GearTeethPocketDiameter * 2
  sketch-geometry (2):
    g0: Circle CenterX=0 CenterY=0 CenterZ=0 NormalX=0 NormalY=0 NormalZ=1 AngleXU=0 Radius=9
    g1: Circle CenterX=0 CenterY=0 CenterZ=0 NormalX=0 NormalY=0 NormalZ=1 AngleXU=0 Radius=18
  constraints (4):
    c: Coincident(g0,g-1)
    c: Diameter(g0) = 18
    c: Coincident(g1,g0)
    c: Diameter(g1) = 36
FEATURE [PartDesign::Pocket] Pocket015  label="TeethPocket001"
  BaseFeature = -> BevelGear002
  Direction = (0,0,-1)
  Length = 5
  Length2 = 5
  Profile = -> Sketch035
  ReferenceAxis = -> Sketch035 [N_Axis]
  Reversed = true
  Type = 1
FEATURE [PartDesign::CoordinateSystem] Back006
  AttacherType = Attacher::AttachEngine3D
  MapMode = 11
  Placement = pos=(0,0,0) rot=(0,0,1;3.73186rad)
  Support = -> [Pocket015]
FEATURE [Sketcher::SketchObject] Sketch036
  FullyConstrained = true
  MapMode = 5
  Support = -> [XY_Plane034]
  expr: Constraints[2] = Spreadsheet.GearTeethPocketDiameter * 2
  expr: Constraints[3] = Spreadsheet.GearTeethPocketDiameter
  sketch-geometry (2):
    g0: Circle CenterX=0 CenterY=0 CenterZ=0 NormalX=0 NormalY=0 NormalZ=1 AngleXU=0 Radius=18
    g1: Circle CenterX=0 CenterY=0 CenterZ=0 NormalX=0 NormalY=0 NormalZ=1 AngleXU=0 Radius=9
  constraints (4):
    c: Coincident(g0,g-1)
    c: Coincident(g1,g0)
    c: Diameter(g0) = 36
    c: Diameter(g1) = 18
FEATURE [PartDesign::CoordinateSystem] Gear
  AttacherType = Attacher::AttachEngine3D
  MapMode = 11
  Placement = pos=(0,0,0) rot=(0,0,1;1.5708rad)
  Support = -> [Pad012]
FEATURE [Sketcher::SketchObject] Sketch034
  FullyConstrained = true
  MapMode = 5
  Support = -> [XY_Plane034]
  expr: Constraints[4] = Spreadsheet.ShaftCouplerInnerDiameter
  expr: Constraints[5] = Spreadsheet.ShaftCouplerInnerDiameter / 2 - 1
  sketch-geometry (2):
    g0: ArcOfCircle CenterX=0 CenterY=0 CenterZ=0 NormalX=0 NormalY=0 NormalZ=1 AngleXU=0 Radius=4.075 StartAngle=2.28655 EndAngle=7.13823
    g1: LineSegment StartX=-2.67395 StartY=3.075 StartZ=0 EndX=2.67395 EndY=3.075 EndZ=0
  constraints (6):
    c: Coincident(g0,g-1)
    c: Horizontal(g1)
    c: Coincident(g0,g1)
    c: Coincident(g0,g1)
    c: Diameter(g0) = 8.15
    c: DistanceY(g0,g0) = 3.075
FEATURE [PartDesign::Pocket] Pocket013  label="ShaftPocket002"
  BaseFeature = -> Pad013
  Direction = (0,0,-1)
  Length = 11
  Length2 = 5
  Profile = -> Sketch034
  ReferenceAxis = -> Sketch034 [N_Axis]
  Type = 1
  expr: Length = Spreadsheet.GearShaftPocketDepth
FEATURE [PartDesign::Chamfer] Chamfer003  label="ShaftChamfer"
  Angle = 45
  Base = -> Pocket013 [Edge6,Edge7]
  BaseFeature = -> Pocket013
  ChamferType = 0
  FlipDirection = false
  Size = 0.3
  Size2 = 1
  SupportTransform = false
  UseAllEdges = false
FEATURE [PartDesign::FeaturePython] BevelGear003  # WARN: FeaturePython — macro-defined, semantics opaque (R4)
  AttacherType = Attacher::AttachEngine3D
  BaseFeature = -> Chamfer003
  angular_backlash = 0
  backlash = 0
  beta = 0
  clearance = 0.1
  dw = 18
  height = 8
  module = 1
  numpoints = 6
  pitch_angle = 45
  pressure_angle = 20
  reset_origin = true
  teeth = 18
  version = 0.0.4
  expr: angular_backlash = backlash / dw * 360° / pi
  expr: beta = Spreadsheet.GearHelix
  expr: dw = teeth * module
  expr: height = Spreadsheet.GearHeight
  expr: module = Spreadsheet.GearModule
  expr: teeth = Spreadsheet.GearTeeth
FEATURE [PartDesign::Pocket] Pocket016  label="TeethPocket"
  BaseFeature = -> BevelGear003
  Direction = (0,0,-1)
  Length = 5
  Length2 = 5
  Profile = -> Sketch036
  ReferenceAxis = -> Sketch036 [N_Axis]
  Reversed = true
  Type = 1
FEATURE [PartDesign::CoordinateSystem] Gear003
  AttacherType = Attacher::AttachEngine3D
  MapMode = 11
  Placement = pos=(0,0,0) rot=(0,0,1;1.5708rad)
  Support = -> [Chamfer003]
FEATURE [PartDesign::Pocket] Pocket017  label="GearShaftPocket"
  BaseFeature = -> Pocket016
  Direction = (0,0,-1)
  Length = 5
  Length2 = 5
  Profile = -> Pocket016 [Face35]
  Type = 1
FEATURE [Sketcher::SketchObject] Sketch037
  AttachmentOffset = pos=(0,0,-9) rot=(0,0,1;0rad)
  FullyConstrained = true
  MapMode = 5
  Placement = pos=(0,9,2e-15) rot=(1,0,0;1.5708rad)
  Support = -> [XZ_Plane034]
  expr: .AttachmentOffset.Base.z = -Spreadsheet.GearTeethPocketDiameter / 2
  expr: Constraints[2] = Spreadsheet.GearLockBoltThreadDiameter
  expr: Constraints[4] = Spreadsheet.GearLockBoltSeparation
  expr: Constraints[5] = Spreadsheet.GearLockBoltPosition
  sketch-geometry (2):
    g0: Circle CenterX=0 CenterY=-4 CenterZ=0 NormalX=0 NormalY=0 NormalZ=1 AngleXU=0 Radius=2.1
    g1: Circle CenterX=0 CenterY=-12 CenterZ=0 NormalX=0 NormalY=0 NormalZ=1 AngleXU=0 Radius=2.1
  constraints (6):
    c: PointOnObject(g0,g-2)
    c: PointOnObject(g1,g-2)
    c: Diameter(g0) = 4.2
    c: Equal(g0,g1)
    c: DistanceY(g1,g0) = 8
    c: DistanceY(g0,g-1) = 4
FEATURE [PartDesign::Pocket] Pocket018  label="LockBoltPocket021"
  BaseFeature = -> Pocket017
  Direction = (0,1,2e-16)
  Length = 9
  Length2 = 5
  Profile = -> Sketch037
  ReferenceAxis = -> Sketch037 [N_Axis]
  Reversed = true
  Type = 0
  expr: Length = Spreadsheet.GearTeethPocketDiameter / 2
FEATURE [PartDesign::Body] Body012
  Group = -> [Sketch033,Pad013,Sketch034,Pocket013,Chamfer003,BevelGear003,Sketch036,Pocket016,Pocket017,Sketch037,Pocket018]
  Origin = -> Origin034
  Tip = -> Pocket018
FEATURE [App::Part] Part010  label="BevelGearBLDC"
  Group = -> [Body012,Back006,Gear003]
  Origin = -> Origin033
FEATURE [PartDesign::Pocket] Pocket019  label="GearPocket"
  BaseFeature = -> Pocket015
  Direction = (0,0,-1)
  Length = 5
  Length2 = 5
  Profile = -> Pocket015 [Face35]
  Type = 1
FEATURE [Sketcher::SketchObject] Sketch038  label="LockBoltPocket"
  AttachmentOffset = pos=(0,0,-8) rot=(0,0,1;0rad)
  FullyConstrained = true
  MapMode = 5
  Placement = pos=(0,8,1.8e-15) rot=(1,0,0;1.5708rad)
  Support = -> [XZ_Plane032]
  expr: .AttachmentOffset.Base.z = -Spreadsheet.GearShaftOuterDiameter / 2
  expr: Constraints[1] = Spreadsheet.GearLockBoltThreadDiameter
  expr: Constraints[2] = Spreadsheet.GearShaftLength / 2
  sketch-geometry (1):
    g0: Circle CenterX=0 CenterY=-3 CenterZ=0 NormalX=0 NormalY=0 NormalZ=1 AngleXU=0 Radius=2.1
  constraints (3):
    c: PointOnObject(g0,g-2)
    c: Diameter(g0) = 4.2
    c: DistanceY(g0,g-1) = 3
FEATURE [PartDesign::Pocket] Pocket020  label="LockBoltPocket020"
  BaseFeature = -> Pocket019
  Direction = (0,1,2e-16)
  Length = 8
  Length2 = 5
  Profile = -> Sketch038
  ReferenceAxis = -> Sketch038 [N_Axis]
  Reversed = true
  Type = 0
  expr: Length = Spreadsheet.GearShaftOuterDiameter / 2
FEATURE [PartDesign::Body] Body011
  Group = -> [Sketch031,Pad012,Sketch032,Pocket011,Chamfer002,BevelGear002,Sketch035,Pocket015,Pocket019,Sketch038,Pocket020]
  Origin = -> Origin032
  Placement = pos=(0,0,0) rot=(0,0,1;0.139626rad)
  Tip = -> Pocket020
FEATURE [App::Part] Part009  label="BevelGearSpindle"
  Group = -> [Body011,Back005,Gear]
  Origin = -> Origin031
FEATURE [App::Link] Link001  label="TopSlide"
  LinkedObject = -> <external ToolPost.FCStd>#Part
FEATURE [App::Link] TopSlide  label="TopSlide001"
  AssemblyType = Part::Link
  AttachedBy = #ToolBackRight
  AttachedTo = Housing#BackBearing
  AttachmentOffset = pos=(-12.5,10,-4) rot=(-0.57735,-0.57735,-0.57735;2.0944rad)
  LinkPlacement = pos=(-34,-7,20.75) rot=(0,0,1;4.71239rad)
  LinkedObject = -> <external ToolPost.FCStd>#Part
  Placement = pos=(-34,-7,20.75) rot=(0,0,1;4.71239rad)
  SolverId = Asm4EE
  expr: Placement = Housing.Placement * BackBearing.Placement * AttachmentOffset * ToolPost#ToolBackRight.Placement ^ -1
FEATURE [Sketcher::SketchObject] Sketch039
  FullyConstrained = true
  MapMode = 5
  Support = -> [XY_Plane036]
  expr: Constraints[1] = Spreadsheet.GearShaftOuterDiameter
  sketch-geometry (1):
    g0: Circle CenterX=0 CenterY=0 CenterZ=0 NormalX=0 NormalY=0 NormalZ=1 AngleXU=0 Radius=8
  constraints (2):
    c: Coincident(g0,g-1)
    c: Diameter(g0) = 16
FEATURE [PartDesign::Pad] Pad014
  Direction = (0,0,1)
  Length = 6
  Length2 = 10
  Profile = -> Sketch039
  ReferenceAxis = -> Sketch039 [N_Axis]
  Reversed = true
  Type = 0
  expr: Length = Spreadsheet.GearLengthSpindle - Spreadsheet.GearHeight
FEATURE [Sketcher::SketchObject] Sketch040
  AttachmentOffset = pos=(0,0,-6) rot=(0,0,1;0rad)
  FullyConstrained = true
  MapMode = 5
  Placement = pos=(0,0,-6) rot=(0,0,1;0rad)
  Support = -> [XY_Plane036]
  expr: .AttachmentOffset.Base.z = -Spreadsheet.GearShaftLength
  expr: Constraints[4] = Spreadsheet.ShaftCouplerInnerDiameter
  expr: Constraints[5] = Spreadsheet.ShaftCouplerInnerDiameter / 2 - 1
  sketch-geometry (2):
    g0: ArcOfCircle CenterX=0 CenterY=0 CenterZ=0 NormalX=0 NormalY=0 NormalZ=1 AngleXU=0 Radius=4.075 StartAngle=2.28655 EndAngle=7.13823
    g1: LineSegment StartX=-2.67395 StartY=3.075 StartZ=0 EndX=2.67395 EndY=3.075 EndZ=0
  constraints (6):
    c: Coincident(g0,g-1)
    c: Horizontal(g1)
    c: Coincident(g0,g1)
    c: Coincident(g0,g1)
    c: Diameter(g0) = 8.15
    c: DistanceY(g0,g0) = 3.075
FEATURE [PartDesign::Pocket] Pocket021  label="ShaftPocket003"
  BaseFeature = -> Pad014
  Direction = (0,0,-1)
  Length = 11
  Length2 = 5
  Profile = -> Sketch040
  ReferenceAxis = -> Sketch040 [N_Axis]
  Reversed = true
  Type = 1
  expr: Length = Spreadsheet.GearShaftPocketDepth
FEATURE [PartDesign::Chamfer] Chamfer004  label="Chamferhaft001"
  Angle = 45
  Base = -> Pocket021 [Edge6,Edge7]
  BaseFeature = -> Pocket021
  ChamferType = 0
  FlipDirection = false
  Size = 0.3
  Size2 = 1
  SupportTransform = false
  UseAllEdges = false
FEATURE [PartDesign::CoordinateSystem] Back007
  AttacherType = Attacher::AttachEngine3D
  MapMode = 11
  Placement = pos=(0,0,-6) rot=(0,0,1;1.5708rad)
  Support = -> [Chamfer004]
FEATURE [Sketcher::SketchObject] Sketch042  label="LockBoltPocket023"
  AttachmentOffset = pos=(0,0,-8) rot=(0,0,1;0rad)
  FullyConstrained = true
  MapMode = 5
  Placement = pos=(0,8,1.8e-15) rot=(1,0,0;1.5708rad)
  Support = -> [XZ_Plane036]
  expr: .AttachmentOffset.Base.z = -Spreadsheet.GearShaftOuterDiameter / 2
  expr: Constraints[1] = Spreadsheet.GearLockBoltThreadDiameter
  expr: Constraints[2] = Spreadsheet.GearShaftLength / 2
  sketch-geometry (1):
    g0: Circle CenterX=0 CenterY=-3 CenterZ=0 NormalX=0 NormalY=0 NormalZ=1 AngleXU=0 Radius=2.1
  constraints (3):
    c: PointOnObject(g0,g-2)
    c: Diameter(g0) = 4.2
    c: DistanceY(g0,g-1) = 3
FEATURE [PartDesign::Pocket] Pocket024  label="LockBoltPocket022"
  BaseFeature = -> Chamfer004
  Direction = (0,1,2e-16)
  Length = 8
  Length2 = 5
  Profile = -> Sketch042
  ReferenceAxis = -> Sketch042 [N_Axis]
  Reversed = true
  Type = 0
  expr: Length = Spreadsheet.GearShaftOuterDiameter / 2
FEATURE [PartDesign::FeaturePython] InvoluteGear  # WARN: FeaturePython — macro-defined, semantics opaque (R4)
  AttacherType = Attacher::AttachEngine3D
  BaseFeature = -> Pocket024
  angular_backlash = 0
  backlash = 0
  beta = 0
  clearance = 0.25
  da = 20
  df = 15.5
  double_helix = false
  dw = 18
  head = 0
  head_fillet = 0
  height = 8
  module = 1
  numpoints = 6
  pressure_angle = 20
  properties_from_tool = false
  reversed_backlash = false
  root_fillet = 0
  shift = 0
  simple = false
  teeth = 18
  transverse_pitch = 3.14159
  undercut = false
  version = 0.0.4
  expr: angular_backlash = backlash / dw * 360° / pi
  expr: dw = teeth * module
  expr: height = Spreadsheet.GearHeight
  expr: module = Spreadsheet.GearModule
  expr: teeth = Spreadsheet.GearTeeth
FEATURE [PartDesign::ShapeBinder] ShapeBinder
  Placement = pos=(0,0,-6) rot=(0,0,1;0rad)
  Support = -> [Sketch040]
  TraceSupport = false
FEATURE [PartDesign::Pocket] Pocket025  label="ShaftPocket004"
  BaseFeature = -> InvoluteGear
  Direction = (0,0,-1)
  Length = 5
  Length2 = 5
  Profile = -> ShapeBinder
  Reversed = true
  Type = 1
FEATURE [PartDesign::Body] Body013  label="SpurGear"
  Group = -> [Sketch039,Pad014,Sketch040,Pocket021,Chamfer004,Sketch042,Pocket024,InvoluteGear,ShapeBinder,Pocket025]
  Origin = -> Origin036
  Placement = pos=(0,0,0) rot=(0,0,1;0.139626rad)
  Tip = -> Pocket025
FEATURE [PartDesign::CoordinateSystem] Gear004
  AttacherType = Attacher::AttachEngine3D
  MapMode = 11
  Placement = pos=(0,1.3e-15,8) rot=(0.936643,-0.350285,0;3.14159rad)
  Support = -> [Pocket025]
FEATURE [App::Part] Part011  label="SpurGearSpindle"
  Group = -> [Body013,Back007,Gear004]
  Origin = -> Origin035
FEATURE [App::Link] SpurGearSpindle  label="SpurGearSpindle001"
  AssemblyType = Part::Link
  AttachedBy = #Back007
  AttachedTo = Spindle#Back004
  AttachmentOffset = pos=(0,0,-8) rot=(0,0,1;0rad)
  LinkPlacement = pos=(-3.19e-14,-115,72) rot=(0,-0.707107,0.707107;3.14159rad)
  LinkedObject = -> Part011
  Placement = pos=(-3.19e-14,-115,72) rot=(0,-0.707107,0.707107;3.14159rad)
  SolverId = Asm4EE
  expr: Placement = Spindle.Placement * Back004.Placement * AttachmentOffset * Back007.Placement ^ -1
FEATURE [Sketcher::SketchObject] Sketch045
  FullyConstrained = true
  MapMode = 5
  Support = -> [XY_Plane039]
  expr: Constraints[1] = Spreadsheet.GearShaftOuterDiameter
  sketch-geometry (1):
    g0: Circle CenterX=0 CenterY=0 CenterZ=0 NormalX=0 NormalY=0 NormalZ=1 AngleXU=0 Radius=8
  constraints (2):
    c: Coincident(g0,g-1)
    c: Diameter(g0) = 16
FEATURE [PartDesign::Pad] Pad016
  Direction = (0,0,1)
  Length = 16
  Length2 = 10
  Profile = -> Sketch045
  ReferenceAxis = -> Sketch045 [N_Axis]
  Reversed = true
  Type = 0
  expr: Length = Spreadsheet.GearLengthBLDC - Spreadsheet.GearHeight
FEATURE [Sketcher::SketchObject] Sketch046
  FullyConstrained = true
  MapMode = 5
  Support = -> [XY_Plane039]
  expr: Constraints[4] = Spreadsheet.ShaftCouplerInnerDiameter
  expr: Constraints[5] = Spreadsheet.ShaftCouplerInnerDiameter / 2 - 1
  sketch-geometry (2):
    g0: ArcOfCircle CenterX=0 CenterY=0 CenterZ=0 NormalX=0 NormalY=0 NormalZ=1 AngleXU=0 Radius=4.075 StartAngle=2.28655 EndAngle=7.13823
    g1: LineSegment StartX=-2.67395 StartY=3.075 StartZ=0 EndX=2.67395 EndY=3.075 EndZ=0
  constraints (6):
    c: Coincident(g0,g-1)
    c: Horizontal(g1)
    c: Coincident(g0,g1)
    c: Coincident(g0,g1)
    c: Diameter(g0) = 8.15
    c: DistanceY(g0,g0) = 3.075
FEATURE [PartDesign::Pocket] Pocket027  label="ShaftPocket006"
  BaseFeature = -> Pad016
  Direction = (0,0,-1)
  Length = 11
  Length2 = 5
  Profile = -> Sketch046
  ReferenceAxis = -> Sketch046 [N_Axis]
  Type = 1
  expr: Length = Spreadsheet.GearShaftPocketDepth
FEATURE [PartDesign::Chamfer] Chamfer006  label="ShaftChamfer001"
  Angle = 45
  Base = -> Pocket027 [Edge6,Edge7]
  BaseFeature = -> Pocket027
  ChamferType = 0
  FlipDirection = false
  Size = 0.3
  Size2 = 1
  SupportTransform = false
  UseAllEdges = false
FEATURE [Sketcher::SketchObject] Sketch049
  AttachmentOffset = pos=(0,0,-9) rot=(0,0,1;0rad)
  FullyConstrained = true
  MapMode = 5
  Placement = pos=(0,9,2e-15) rot=(1,0,0;1.5708rad)
  Support = -> [XZ_Plane038]
  expr: .AttachmentOffset.Base.z = -Spreadsheet.GearTeethPocketDiameter / 2
  expr: Constraints[2] = Spreadsheet.GearLockBoltThreadDiameter
  expr: Constraints[4] = Spreadsheet.GearLockBoltSeparation
  expr: Constraints[5] = Spreadsheet.GearLockBoltPosition
  sketch-geometry (2):
    g0: Circle CenterX=0 CenterY=-4 CenterZ=0 NormalX=0 NormalY=0 NormalZ=1 AngleXU=0 Radius=2.1
    g1: Circle CenterX=0 CenterY=-12 CenterZ=0 NormalX=0 NormalY=0 NormalZ=1 AngleXU=0 Radius=2.1
  constraints (6):
    c: PointOnObject(g0,g-2)
    c: PointOnObject(g1,g-2)
    c: Diameter(g0) = 4.2
    c: Equal(g0,g1)
    c: DistanceY(g1,g0) = 8
    c: DistanceY(g0,g-1) = 4
FEATURE [PartDesign::Pocket] Pocket031  label="LockBoltPocket024"
  BaseFeature = -> Chamfer006
  Direction = (0,1,2e-16)
  Length = 9
  Length2 = 5
  Profile = -> Sketch049
  ReferenceAxis = -> Sketch049 [N_Axis]
  Reversed = true
  Type = 0
  expr: Length = Spreadsheet.GearTeethPocketDiameter / 2
FEATURE [PartDesign::FeaturePython] InvoluteGear002  # WARN: FeaturePython — macro-defined, semantics opaque (R4)
  AttacherType = Attacher::AttachEngine3D
  BaseFeature = -> Pocket031
  angular_backlash = 0
  backlash = 0
  beta = 0
  clearance = 0.25
  da = 20
  df = 15.5
  double_helix = false
  dw = 18
  head = 0
  head_fillet = 0
  height = 8
  module = 1
  numpoints = 6
  pressure_angle = 20
  properties_from_tool = false
  reversed_backlash = false
  root_fillet = 0
  shift = 0
  simple = false
  teeth = 18
  transverse_pitch = 3.14159
  undercut = false
  version = 0.0.4
  expr: angular_backlash = backlash / dw * 360° / pi
  expr: dw = teeth * module
  expr: height = Spreadsheet.GearHeight
  expr: module = Spreadsheet.GearModule
  expr: teeth = Spreadsheet.GearTeeth
FEATURE [PartDesign::ShapeBinder] ShapeBinder001  label="ShaftPocket007"
  Support = -> [Sketch046]
  TraceSupport = false
FEATURE [PartDesign::Pocket] Pocket032
  BaseFeature = -> InvoluteGear002
  Direction = (0,0,-1)
  Length = 5
  Length2 = 5
  Profile = -> ShapeBinder001
  Reversed = true
  Type = 1
FEATURE [PartDesign::CoordinateSystem] Back008
  AttacherType = Attacher::AttachEngine3D
  MapMode = 11
  Placement = pos=(0,0,-16) rot=(0,0,1;1.5708rad)
  Support = -> [Pocket032]
FEATURE [PartDesign::Body] Body014
  Group = -> [Sketch045,Pad016,Sketch046,Pocket027,Chamfer006,Sketch049,Pocket031,InvoluteGear002,ShapeBinder001,Pocket032]
  Origin = -> Origin038
  Tip = -> Pocket032
FEATURE [PartDesign::CoordinateSystem] Gear005
  AttacherType = Attacher::AttachEngine3D
  AttachmentOffset = pos=(0,0,0) rot=(0,0,1;0.10472rad)
  MapMode = 11
  Placement = pos=(0,1.3e-15,8) rot=(0.917027,-0.398825,0;3.14159rad)
  Support = -> [Pocket032]
FEATURE [App::Part] Part012  label="SpurGearBLDC"
  Group = -> [Body014,Back008,Gear005]
  Origin = -> Origin037
FEATURE [App::Link] SpurGearBLDC  label="SpurGearBLDC001"
  AssemblyType = Part::Link
  AttachedBy = #Back008
  AttachedTo = BLDCmotor#ShaftTop
  AttachmentOffset = pos=(0,0,-24) rot=(0,0,1;0rad)
  LinkPlacement = pos=(-2.74e-14,-123,90) rot=(-0.57735,-0.57735,-0.57735;2.0944rad)
  LinkedObject = -> Part012
  Placement = pos=(-2.74e-14,-123,90) rot=(-0.57735,-0.57735,-0.57735;2.0944rad)
  SolverId = Asm4EE
  expr: Placement = BLDCmotor.Placement * ShaftTop.Placement * AttachmentOffset * Back008.Placement ^ -1
FEATURE [Part::Feature] Part__Feature006  label="42BLS80-24-01"
  shape: bbox 42 x 64.1 x 112.7 mm, 281 faces (baked)
FEATURE [PartDesign::CoordinateSystem] Shaft  label="Shaft001"
  AttacherType = Attacher::AttachEngine3D
  MapMode = 11
  Placement = pos=(0,0,99.2) rot=(0.707107,0.707107,0;3.14159rad)
  Support = -> [Part__Feature006]
FEATURE [PartDesign::CoordinateSystem] Flange001
  AttacherType = Attacher::AttachEngine3D
  MapMode = 11
  Placement = pos=(0.103987,1.6e-15,79.2) rot=(0.707107,0.707107,0;3.14159rad)
  Support = -> [Part__Feature006]
FEATURE [App::Part] Part  label="BLDC 42mm"
  Group = -> [Part__Feature006,Shaft,Flange001]
  Origin = -> Origin039
FEATURE [App::Link] BLDC_42mm  label="BLDC 42mm001"
  AssemblyType = Part::Link
  AttachedBy = #Shaft
  AttachedTo = Spindle#Back004
  AttachmentOffset = pos=(0,0,2) rot=(0,0,1;0rad)
  LinkPlacement = pos=(-9.35e-14,-218.2,72) rot=(1,0,0;4.71239rad)
  LinkedObject = -> Part
  Placement = pos=(-9.35e-14,-218.2,72) rot=(1,0,0;4.71239rad)
  SolverId = Asm4EE
  expr: Placement = Spindle.Placement * Back004.Placement * AttachmentOffset * Shaft.Placement ^ -1
FEATURE [App::Link] Link002  label="ConnectorHousing"
  LinkedObject = -> <external ConnectorHousing.FCStd>#Part
FEATURE [App::Link] ConnectorHousing  label="ConnectorHousing001"
  AssemblyType = Part::Link
  AttachedBy = #Back
  AttachedTo = BLDCmotor#Back009
  AttachmentOffset = pos=(-27,0,45) rot=(0,0,-1;3.14159rad)
  LinkPlacement = pos=(-9.06e-14,-209.8,90.7121) rot=(0,0,-1;4.71239rad)
  LinkedObject = -> <external ConnectorHousing.FCStd>#Part
  Placement = pos=(-9.06e-14,-209.8,90.7121) rot=(0,0,-1;4.71239rad)
  SolverId = Asm4EE
  expr: Placement = BLDCmotor.Placement * Back009.Placement * AttachmentOffset * ConnectorHousing#Back.Placement ^ -1
FEATURE [App::Part] Model
  AssemblyType = Part::Link
  Group = -> [LCS_Origin,Constraints,Variables,Configurations,Housing,Bearing002,Bearing003,Spindle,BLDCmotor,SpacerFront,LockNut001,BLDC_adapter,BevelGearSpindle,BevelGearBLDC,TopSlide,SpurGearSpindle,SpurGearBLDC,BLDC_42mm,ConnectorHousing]
  Origin = -> Origin007
  Type = Assembly
FEATURE [PartDesign::CoordinateSystem] Back009
  AttacherType = Attacher::AttachEngine3D
  MapMode = 11
  Placement = pos=(0,0,0.3) rot=(0,0,1;1.5708rad)
  Support = -> [Part__Feature]
FEATURE [App::Part] Part005  label="BLDCmotor"
  Group = -> [Part__Feature,Flange,ShaftTop,Back009]
  Origin = -> Origin017
FEATURE [App::DocumentObjectGroup] Parts
  Group = -> [Part001,Bearing001,Part003,Part005,Part006,LockNut,Link,Part009,Part010,Link001,Part011,Part012,Link002,Part]
FEATURE [Sketcher::SketchObject] Sketch050
  FullyConstrained = false
  MapMode = 5
  Support = -> [XY_Plane042]
  sketch-geometry (9):
    g0: ArcOfCircle CenterX=-3.86982 CenterY=0 CenterZ=0 NormalX=0 NormalY=0 NormalZ=1 AngleXU=0 Radius=2.75 StartAngle=3.79337 EndAngle=5.6314
    g1: ArcOfCircle CenterX=3.86982 CenterY=0 CenterZ=0 NormalX=0 NormalY=0 NormalZ=1 AngleXU=0 Radius=3.05 StartAngle=3.72029 EndAngle=5.70448
    g2: ArcOfCircle CenterX=0 CenterY=0 CenterZ=0 NormalX=0 NormalY=0 NormalZ=1 AngleXU=0 Radius=7 StartAngle=3.38222 EndAngle=6.04256
    g3: LineSegment StartX=-1.68356 StartY=-1.66816 StartZ=0 EndX=1.31644 EndY=-1.66816 EndZ=0
    g4: LineSegment StartX=-6.05608 StartY=-1.66816 StartZ=0 EndX=-6.79833 EndY=-1.66816 EndZ=0
    g5: LineSegment StartX=6.4232 StartY=-1.66816 StartZ=0 EndX=6.79833 EndY=-1.66816 EndZ=0
    g6: LineSegment StartX=-6.79833 StartY=-1.66816 StartZ=0 EndX=-6.79833 EndY=0 EndZ=0
    g7: LineSegment StartX=1.31644 StartY=-1.66816 StartZ=0 EndX=1.31644 EndY=0 EndZ=0
    g8: LineSegment StartX=6.79833 StartY=-1.66816 StartZ=0 EndX=6.79833 EndY=0 EndZ=0
  constraints (27):
    c: PointOnObject(g0,g-1)
    c: Diameter(g0) = 5.5
    c: Diameter(g1) = 6.1
    c: Symmetric(g0,g1,g-1)
    c: Coincident(g2,g-1)
    c: Diameter(g2) = 14
    c: Horizontal(g3)
    c: DistanceX(g3,g3) = 3
    c: Horizontal(g4)
    c: Coincident(g6,g4)
    c: PointOnObject(g6,g-1)
    c: Vertical(g6)
    c: Coincident(g7,g3)
    c: PointOnObject(g7,g-1)
    c: Coincident(g8,g5)
    c: PointOnObject(g8,g-1)
    c: Vertical(g8)
    c: Vertical(g7)
    c: Equal(g6,g7)
    c: Equal(g7,g8)
    c: Horizontal(g5)
    c: Coincident(g2,g5)
    c: Coincident(g2,g4)
    c: Coincident(g0,g3)
    c: Coincident(g0,g4)
    c: Coincident(g1,g3)
    c: Coincident(g1,g5)
FEATURE [PartDesign::Pad] Pad017
  Direction = (0,0,1)
  Length = 10
  Length2 = 10
  Profile = -> Sketch050
  ReferenceAxis = -> Sketch050 [N_Axis]
  Type = 0
FEATURE [Sketcher::SketchObject] Sketch051
  FullyConstrained = true
  MapMode = 5
  Placement = pos=(0,-1.66816,0) rot=(0,0.707107,0.707107;3.14159rad)
  sketch-geometry (1):
    g0: Circle CenterX=0 CenterY=5 CenterZ=0 NormalX=0 NormalY=0 NormalZ=1 AngleXU=0 Radius=1.25
  constraints (3):
    c: PointOnObject(g0,g-2)
    c: Diameter(g0) = 2.5
    c: DistanceY(g-1,g0) = 5
FEATURE [PartDesign::Pocket] Pocket033
  BaseFeature = -> Pad017
  Direction = (0,-1,2e-16)
  Length = 5
  Length2 = 5
  Profile = -> Sketch051
  ReferenceAxis = -> Sketch051 [N_Axis]
  Type = 1
FEATURE [PartDesign::Body] Body015
  Group = -> [Sketch050,Pad017,Sketch051,Pocket033]
  Origin = -> Origin041
  Tip = -> Pocket033
FEATURE [App::Part] Part013  label="CableLock"
  Group = -> [Body015]
  Origin = -> Origin040
FEATURE [TechDraw::DrawViewPart] View011  label="LockNut FV"
  CoarseView = false
  Direction = (0,0,1)
  Focus = 100
  HardHidden = false
  IsoCount = 0
  IsoHidden = false
  IsoVisible = false
  LockPosition = false
  Perspective = false
  Rotation = 0
  ScaleType = 0
  SeamHidden = false
  SeamVisible = true
  SmoothHidden = false
  SmoothVisible = true
  Source = -> [LockNut]
  X = 126.437
  XDirection = (1,0,0)
  Y = 87.6657
FEATURE [TechDraw::DrawViewPart] View012  label="Lock Nut TV"
  CoarseView = false
  Direction = (0,-1,0)
  Focus = 100
  HardHidden = false
  IsoCount = 0
  IsoHidden = false
  IsoVisible = false
  LockPosition = false
  Perspective = false
  Rotation = 0
  ScaleType = 0
  SeamHidden = false
  SeamVisible = true
  SmoothHidden = false
  SmoothVisible = true
  Source = -> [LockNut]
  X = 38.1493
  XDirection = (1,0,0)
  Y = 90.906
FEATURE [TechDraw::DrawViewDimension] Dimension066
  AngleOverride = false
  Arbitrary = false
  ArbitraryTolerances = false
  EqualTolerance = true
  ExtensionAngle = 0
  FormatSpec = %.2f
  FormatSpecOverTolerance = %+.2f
  FormatSpecUnderTolerance = %+.2f
  Inverted = false
  LineAngle = 0
  LockPosition = false
  MeasureType = 1
  OverTolerance = 0
  References2D = -> [View011]
  Rotation = 0
  ScaleType = 0
  TheoreticalExact = false
  Type = 1
  UnderTolerance = 0
  X = 0
  Y = 14.6367
FEATURE [TechDraw::DrawViewDimension] Dimension067
  AngleOverride = false
  Arbitrary = false
  ArbitraryTolerances = false
  EqualTolerance = true
  ExtensionAngle = 0
  FormatSpec = %.2f
  FormatSpecOverTolerance = %+.2f
  FormatSpecUnderTolerance = %+.2f
  Inverted = false
  LineAngle = 0
  LockPosition = false
  MeasureType = 1
  OverTolerance = 0
  References2D = -> [View011]
  Rotation = 0
  ScaleType = 0
  TheoreticalExact = false
  Type = 1
  UnderTolerance = 0
  X = -0.495854
  Y = 23.6571
FEATURE [TechDraw::DrawViewDimension] Dimension068
  AngleOverride = false
  Arbitrary = false
  ArbitraryTolerances = false
  EqualTolerance = true
  ExtensionAngle = 0
  FormatSpec = %.2f
  FormatSpecOverTolerance = %+.2f
  FormatSpecUnderTolerance = %+.2f
  Inverted = false
  LineAngle = 0
  LockPosition = false
  MeasureType = 1
  OverTolerance = 0
  References2D = -> [View011]
  Rotation = 0
  ScaleType = 0
  TheoreticalExact = false
  Type = 2
  UnderTolerance = 0
  X = 23.3955
  Y = 15.0602
FEATURE [TechDraw::DrawViewDimension] Dimension069
  AngleOverride = false
  Arbitrary = false
  ArbitraryTolerances = false
  EqualTolerance = true
  ExtensionAngle = 0
  FormatSpec = %.2f
  FormatSpecOverTolerance = %+.2f
  FormatSpecUnderTolerance = %+.2f
  Inverted = false
  LineAngle = 0
  LockPosition = false
  MeasureType = 1
  OverTolerance = 0
  References2D = -> [View011]
  Rotation = 0
  ScaleType = 0
  TheoreticalExact = false
  Type = 2
  UnderTolerance = 0
  X = 19.4287
  Y = -16.0692
FEATURE [TechDraw::DrawViewDimension] Dimension070
  AngleOverride = false
  Arbitrary = false
  ArbitraryTolerances = false
  EqualTolerance = true
  ExtensionAngle = 0
  FormatSpec = %.2f
  FormatSpecOverTolerance = %+.2f
  FormatSpecUnderTolerance = %+.2f
  Inverted = false
  LineAngle = 0
  LockPosition = false
  MeasureType = 1
  OverTolerance = 0
  References2D = -> [View011]
  Rotation = 0
  ScaleType = 0
  TheoreticalExact = false
  Type = 2
  UnderTolerance = 0
  X = -21.7975
  Y = 16.271
FEATURE [TechDraw::DrawViewDimension] Dimension071
  AngleOverride = false
  Arbitrary = true
  ArbitraryTolerances = false
  EqualTolerance = true
  ExtensionAngle = 0
  FormatSpec = M10x1
  FormatSpecOverTolerance = %+.2f
  FormatSpecUnderTolerance = %+.2f
  Inverted = false
  LineAngle = 0
  LockPosition = false
  MeasureType = 1
  OverTolerance = 0
  References2D = -> [View012]
  Rotation = 0
  ScaleType = 0
  TheoreticalExact = false
  Type = 5
  UnderTolerance = 0
  X = 32.6435
  Y = -10.4629
FEATURE [TechDraw::DrawViewDimension] Dimension072
  AngleOverride = false
  Arbitrary = true
  ArbitraryTolerances = false
  EqualTolerance = true
  ExtensionAngle = 0
  FormatSpec = M3
  FormatSpecOverTolerance = %+.2f
  FormatSpecUnderTolerance = %+.2f
  Inverted = false
  LineAngle = 0
  LockPosition = false
  MeasureType = 1
  OverTolerance = 0
  References2D = -> [View012]
  Rotation = 0
  ScaleType = 0
  TheoreticalExact = false
  Type = 5
  UnderTolerance = 0
  X = 28.1696
  Y = 4.01724
FEATURE [TechDraw::DrawViewDimension] Dimension073
  AngleOverride = false
  Arbitrary = false
  ArbitraryTolerances = false
  EqualTolerance = true
  ExtensionAngle = 0
  FormatSpec = %.2f
  FormatSpecOverTolerance = %+.2f
  FormatSpecUnderTolerance = %+.2f
  Inverted = false
  LineAngle = 0
  LockPosition = false
  MeasureType = 1
  OverTolerance = 0
  References2D = -> [View012]
  Rotation = 0
  ScaleType = 0
  TheoreticalExact = false
  Type = 1
  UnderTolerance = 0
  X = 2.33522
  Y = 20.9753
FEATURE [TechDraw::DrawViewDimension] Dimension074
  AngleOverride = false
  Arbitrary = false
  ArbitraryTolerances = false
  EqualTolerance = true
  ExtensionAngle = 0
  FormatSpec = ⌀%.2f
  FormatSpecOverTolerance = %+.2f
  FormatSpecUnderTolerance = %+.2f
  Inverted = false
  LineAngle = 0
  LockPosition = false
  MeasureType = 1
  OverTolerance = 0
  References2D = -> [View012]
  Rotation = 0
  ScaleType = 0
  TheoreticalExact = false
  Type = 5
  UnderTolerance = 0
  X = 30.3305
  Y = -17.5598
FEATURE [TechDraw::DrawViewDimension] Dimension075
  AngleOverride = false
  Arbitrary = false
  ArbitraryTolerances = false
  EqualTolerance = true
  ExtensionAngle = 0
  FormatSpec = %.2f
  FormatSpecOverTolerance = %+.2f
  FormatSpecUnderTolerance = %+.2f
  Inverted = false
  LineAngle = 0
  LockPosition = false
  MeasureType = 1
  OverTolerance = 0
  References2D = -> [View011]
  Rotation = 0
  ScaleType = 0
  TheoreticalExact = false
  Type = 2
  UnderTolerance = 0
  X = -31.3298
  Y = 7.29223
FEATURE [TechDraw::DrawPage] Page001  label="SmallParts"
  KeepUpdated = true
  NextBalloonIndex = 1
  ProjectionType = 0
  Template = -> Template001
  Views = -> [View004,Dimension016,Dimension017,SectionView001,Dimension021,Dimension022,Dimension023,View011,View012,Dimension066,Dimension067,Dimension068,Dimension069,Dimension070,Dimension071,Dimension072,Dimension073,Dimension074,Dimension075]
FEATURE [App::DocumentObjectGroup] Group  label="Drawings"
  Group = -> [Page002,Page001,Page]

RESOLVED EXTERNAL PARTS (link-assembly join: the EXTERNAL_REF files above that resolve inside this repo's crawl, each included once):
---- part ConnectorHousing.FCStd = doc fcstd_ba1187c70230 ----
FCSTD DOCUMENT  (FreeCAD 0.21R31155 (Git))
Label: ConnectorHousing
License: All rights reserved
LicenseURL: http://en.wikipedia.org/wiki/All_rights_reserved
objects: Sketcher::SketchObject×10, PartDesign::Pocket×7, PartDesign::Pad×4, PartDesign::Body×4, PartDesign::SubShapeBinder×2, App::Part×2, PartDesign::Fillet×2, PartDesign::CoordinateSystem×2, Spreadsheet::Sheet×1, PartDesign::Revolution×1, App::TextDocument×1, PartDesign::Chamfer×1
note: 48 computed .brp shape members not serialized (recipe doc carries the construction recipe); baked Part::Feature solids carry a one-line shape summary decoded from their .brp

FEATURE [Spreadsheet::Sheet] Spreadsheet
  cells = A4=Dimensions; A5=ConnectorOuterDiameter; B5(ConnectorOuterDiameter)=22; A6=ConnectorPocketDiameter; B6(ConnectorPocketDiameter)=22; A7=ConnectorThreadDiameter; B7(ConnectorThreadDiameter)=18.03; A8=ConnectorThreadLength; B8(ConnectorThreadLength)=11; A9=ThreadPitch; B9(ThreadPitch)=1; A11=BLDCdiameterMount; B11(BLDCdiameterMount)=56.82; A12=BLDCdiameterMotor; B12(BLDCdiameterMotor)=55; A13=BLDCMountThickness; B13(BLDCMountThickness)=18.2; A14=BLDCMotorThickness; B14(BLDCMotorThickness)=20; A15=BLDCWallThicknes; B15(BLDCWallThicknes)=3; A16=BLCDOverhangThickness; B16(BLCDOverhangThickness)==BLDCWallThicknes; A17=BLDCMountIncludedAngel; B17(BLDCMountIncludedAngel)==MountWidth / (MountOuterDiameter * pi) * 360; A18=BLDCbaseThickness; B18(BLDCbaseThickness)=5; A19=BLDCBaseGlueWidth; B19(BLDCBaseGlueWidth)==MountingBoltThreadDiameter + 3; A21=PositionHoleDiameter; B21(PositionHoleDiameter)=3; A22=PositionHolePocketDepth; B22(PositionHolePocketDepth)==PositionBodyThickness + 0.1; A23=PositionBodyThickness; B23(PositionBodyThickness)=3; A25=MountingBoltThreadDiameter; B25(MountingBoltThreadDiameter)=2.5; A26=MountingBoltPocketDepth; B26(MountingBoltPocketDepth)==BLDCbaseThickness + 0.3; A27=CableClearance; B27(CableClearance)=8; A28=CablePocketLength; B28(CablePocketLength)=35; A30=FiletSize; B30(FiletSize)=1; A32=Calculated Fields; A33=MountOuterDiameter; B33(MountOuterDiameter)==BLDCdiameterMount + BLDCWallThicknes * 2; A34=MountWidth; B34(MountWidth)==ConnectorOuterDiameter + BLDCWallThicknes * 2; A35=MountLength; B35(MountLength)==BLDCWallThicknes + CableClearance + CablePocketLength + BLDCWallThicknes; A36=MountingHoleSeparationH; B36(MountingHoleSeparationH)==MountLength - BLDCBaseGlueWidth; A37=MountingHoleSeparationV; B37(MountingHoleSeparationV)==MountWidth - BLDCBaseGlueWidth; A38=MountingHolePositionH; B38(MountingHolePositionH)==-BLDCWallThicknes + 2 + MountingBoltThreadDiameter / 2; A39=MountPositionZ; B39(MountPositionZ)==BLDCdiameterMount / 2 + BLDCbaseThickness; A40=CablePocketWidth; B40(CablePocketWidth)==MountWidth - BLDCBaseGlueWidth * 2; A42=BasePositionV; B42(BasePositionV)==BLDCdiameterMount / 2 - 1; A43=BodyPositionV; B43(BodyPositionV)==BasePositionV + BLDCbaseThickness + 1; A44=ConnectorClearance; B44(ConnectorClearance)==CableClearance - BLDCbaseThickness - PositionBodyThickness + ConnectorOuterDiameter / 2; A45=ConnectorPositionZ; B45(ConnectorPositionZ)==CableClearance - BLDCbaseThickness + ConnectorPocketDiameter / 2; A46=ConnectorPocketDepth; B46(ConnectorPocketDepth)==MountLength - BLDCWallThicknes; A47=MountOuterDiameter; B47(MountOuterDiameter2)==ConnectorPocketDiameter + BLDCWallThicknes * 2; A48=CablePocketPositionV; B48(CablePocketPosition)=11; A49=CablePocketPositionH; B49(CablePocketPositionH)==ConnectorThreadLength - BLDCWallThicknes; A51=ConnectorBasePocketPositionH; B51(ConnectorBasePocketPositionH)==ConnectorClearance * 2
FEATURE [Sketcher::SketchObject] Sketch
  FullyConstrained = true
  MapMode = 5
  Placement = pos=(0,0,0) rot=(1,0,0;1.5708rad)
  Support = -> [XZ_Plane001]
  expr: Constraints[10] = Spreadsheet.BLDCdiameterMotor / 2
  expr: Constraints[11] = Spreadsheet.BLDCMountThickness
  expr: Constraints[18] = Spreadsheet.BLDCWallThicknes
  expr: Constraints[21] = Spreadsheet.BLDCdiameterMount / 2
  expr: Constraints[22] = Spreadsheet.BLDCWallThicknes
  expr: Constraints[23] = Spreadsheet.MountLength
  sketch-geometry (8):
    g0: LineSegment StartX=-3 StartY=31.41 StartZ=0 EndX=46 EndY=31.41 EndZ=0
    g1: LineSegment StartX=46 StartY=31.41 StartZ=0 EndX=46 EndY=27.5 EndZ=0
    g2: LineSegment StartX=46 StartY=27.5 StartZ=0 EndX=18.2 EndY=27.5 EndZ=0
    g3: LineSegment StartX=18.2 StartY=27.5 StartZ=0 EndX=18.2 EndY=28.41 EndZ=0
    g4: LineSegment StartX=18.2 StartY=28.41 StartZ=0 EndX=0 EndY=28.41 EndZ=0
    g5: LineSegment StartX=-3 StartY=25.41 StartZ=0 EndX=0 EndY=25.41 EndZ=0
    g6: LineSegment StartX=0 StartY=25.41 StartZ=0 EndX=0 EndY=28.41 EndZ=0
    g7: LineSegment StartX=-3 StartY=31.41 StartZ=0 EndX=-3 EndY=25.41 EndZ=0
  constraints (24):
    c: PointOnObject(g4,g-2)
    c: Horizontal(g0)
    c: Coincident(g0,g1)
    c: Vertical(g1)
    c: Coincident(g1,g2)
    c: Horizontal(g2)
    c: Coincident(g2,g3)
    c: Vertical(g3)
    c: Coincident(g3,g4)
    c: Horizontal(g4)
    c: DistanceY(g-1,g2) = 27.5
    c: DistanceX(g4,g4) = 18.2
    c: PointOnObject(g5,g-2)
    c: Horizontal(g5)
    c: Coincident(g5,g6)
    c: Coincident(g7,g0)
    c: Coincident(g7,g5)
    c: Vertical(g7)
    c: DistanceY(g6,g6) = 3
    c: Equal(g6,g5)
    c: Coincident(g6,g4)
    c: DistanceY(g-1,g4) = 28.41
    c: DistanceY(g4,g0) = 3
    c: DistanceX(g0,g0) = 49
FEATURE [PartDesign::Revolution] Revolution  label="RoundBase"
  Angle = 54.0755
  Axis = (1,0,0)
  Base = (0,0,0)
  Midplane = true
  Placement = pos=(0,0,0) rot=(1,0,0;1.5708rad)
  Profile = -> Sketch
  ReferenceAxis = -> X_Axis001
  Reversed = true
  expr: Angle = Spreadsheet.BLDCMountIncludedAngel + 3
FEATURE [Sketcher::SketchObject] Sketch001
  AttachmentOffset = pos=(0,0,28.41) rot=(0,0,1;0rad)
  FullyConstrained = true
  MapMode = 5
  Placement = pos=(0,0,28.41) rot=(0,0,1;0rad)
  Support = -> [XY_Plane001]
  expr: .AttachmentOffset.Base.z = Spreadsheet.BLDCdiameterMount / 2
  expr: Constraints[7] = Spreadsheet.MountLength
  expr: Constraints[8] = Spreadsheet.MountWidth
  expr: Constraints[9] = Spreadsheet.BLDCWallThicknes
  sketch-geometry (8):
    g0: LineSegment StartX=-3 StartY=14 StartZ=0 EndX=46 EndY=14 EndZ=0
    g1: LineSegment StartX=46 StartY=14 StartZ=0 EndX=46 EndY=-14 EndZ=0
    g2: LineSegment StartX=46 StartY=-14 StartZ=0 EndX=-3 EndY=-14 EndZ=0
    g3: LineSegment StartX=-3 StartY=-14 StartZ=0 EndX=-3 EndY=14 EndZ=0
    g4: LineSegment StartX=-8 StartY=19 StartZ=0 EndX=51 EndY=19 EndZ=0
    g5: LineSegment StartX=51 StartY=19 StartZ=0 EndX=51 EndY=-19 EndZ=0
    g6: LineSegment StartX=51 StartY=-19 StartZ=0 EndX=-8 EndY=-19 EndZ=0
    g7: LineSegment StartX=-8 StartY=-19 StartZ=0 EndX=-8 EndY=19 EndZ=0
  constraints (22):
    c: Coincident(g0,g1)
    c: Coincident(g1,g2)
    c: Coincident(g2,g3)
    c: Coincident(g3,g0)
    c: Horizontal(g0)
    c: Horizontal(g2)
    c: Vertical(g1)
    c: DistanceX(g2,g2) = 49
    c: DistanceY(g3,g3) = 28
    c: DistanceX(g2,g-1) = 3
    c: Symmetric(g2,g0,g-1)
    c: Coincident(g4,g5)
    c: Coincident(g5,g6)
    c: Coincident(g6,g7)
    c: Coincident(g7,g4)
    c: Horizontal(g4)
    c: Horizontal(g6)
    c: Vertical(g5)
    c: Symmetric(g6,g4,g-1)
    c: DistanceX(g4,g0) = 5
    c: DistanceX(g0,g4) = 5
    c: DistanceY(g0,g4) = 5
FEATURE [Sketcher::SketchObject] Sketch002
  AttachmentOffset = pos=(0,0,27.41) rot=(0,0,1;0rad)
  FullyConstrained = true
  MapMode = 5
  Placement = pos=(0,0,27.41) rot=(0,0,1;0rad)
  Support = -> [XY_Plane001]
  expr: .AttachmentOffset.Base.z = Spreadsheet.BasePositionV
  expr: Constraints[10] = Spreadsheet.BLDCWallThicknes
  expr: Constraints[8] = Spreadsheet.MountWidth
  expr: Constraints[9] = Spreadsheet.MountLength
  sketch-geometry (4):
    g0: LineSegment StartX=-3 StartY=14 StartZ=0 EndX=46 EndY=14 EndZ=0
    g1: LineSegment StartX=46 StartY=14 StartZ=0 EndX=46 EndY=-14 EndZ=0
    g2: LineSegment StartX=46 StartY=-14 StartZ=0 EndX=-3 EndY=-14 EndZ=0
    g3: LineSegment StartX=-3 StartY=-14 StartZ=0 EndX=-3 EndY=14 EndZ=0
  constraints (11):
    c: Coincident(g0,g1)
    c: Coincident(g1,g2)
    c: Coincident(g2,g3)
    c: Coincident(g3,g0)
    c: Horizontal(g0)
    c: Horizontal(g2)
    c: Vertical(g1)
    c: Symmetric(g2,g0,g-1)
    c: DistanceY(g3,g3) = 28
    c: DistanceX(g0,g0) = 49
    c: DistanceX(g0,g-1) = 3
FEATURE [PartDesign::Pad] Pad  label="FlatBase"
  BaseFeature = -> Revolution
  Direction = (0,0,1)
  Length = 6
  Length2 = 10
  Placement = pos=(0,0,0) rot=(1,0,0;1.5708rad)
  Profile = -> Sketch002
  ReferenceAxis = -> Sketch002 [N_Axis]
  Type = 0
  expr: Length = Spreadsheet.BLDCbaseThickness + 1
FEATURE [Sketcher::SketchObject] Sketch003
  FullyConstrained = false
  MapMode = 5
  Support = -> [XY_Plane001]
  expr: Constraints[11] = Spreadsheet.CablePocketLength
  expr: Constraints[12] = Spreadsheet.CablePocketWidth
  sketch-geometry (5):
    g0: LineSegment StartX=0 StartY=8.5 StartZ=0 EndX=35 EndY=8.5 EndZ=0
    g1: LineSegment StartX=35 StartY=8.5 StartZ=0 EndX=35 EndY=-8.5 EndZ=0
    g2: LineSegment StartX=35 StartY=-8.5 StartZ=0 EndX=0 EndY=-8.5 EndZ=0
    g3: LineSegment StartX=0 StartY=-8.5 StartZ=0 EndX=0 EndY=8.5 EndZ=0
    g4: LineSegment StartX=0 StartY=8.5 StartZ=0 EndX=0 EndY=7.43772 EndZ=0
  constraints (13):
    c: Coincident(g0,g1)
    c: Coincident(g1,g2)
    c: Coincident(g2,g3)
    c: Coincident(g3,g0)
    c: Horizontal(g0)
    c: Horizontal(g2)
    c: Vertical(g1)
    c: Symmetric(g0,g2,g-1)
    c: Coincident(g4,g0)
    c: Vertical(g4)
    c: PointOnObject(g2,g-2)
    c: DistanceX(g0,g0) = 35
    c: DistanceY(g3,g3) = 17
FEATURE [PartDesign::Pocket] Pocket001  label="CablePocket"
  BaseFeature = -> Pad
  Direction = (0,0,-1)
  Length = 30
  Length2 = 5
  Midplane = true
  Placement = pos=(0,0,0) rot=(1,0,0;1.5708rad)
  Profile = -> Sketch003
  ReferenceAxis = -> Sketch003 [N_Axis]
  Type = 1
FEATURE [Sketcher::SketchObject] Sketch004
  AttachmentOffset = pos=(0,0,33.51) rot=(0,0,1;0rad)
  FullyConstrained = true
  MapMode = 5
  Placement = pos=(0,0,33.51) rot=(0,0,1;0rad)
  Support = -> [XY_Plane001]
  expr: .AttachmentOffset.Base.z = Spreadsheet.MountPositionZ + 0.1
  expr: Constraints[10] = Spreadsheet.MountingHolePositionH
  expr: Constraints[18] = Spreadsheet.MountingBoltThreadDiameter
  expr: Constraints[8] = Spreadsheet.MountingHoleSeparationV
  expr: Constraints[9] = Spreadsheet.MountingHoleSeparationH
  sketch-geometry (8):
    g0: LineSegment StartX=0.25 StartY=11.25 StartZ=0 EndX=43.75 EndY=11.25 EndZ=0
    g1: LineSegment StartX=43.75 StartY=11.25 StartZ=0 EndX=43.75 EndY=-11.25 EndZ=0
    g2: LineSegment StartX=43.75 StartY=-11.25 StartZ=0 EndX=0.25 EndY=-11.25 EndZ=0
    g3: LineSegment StartX=0.25 StartY=-11.25 StartZ=0 EndX=0.25 EndY=11.25 EndZ=0
    g4: Circle CenterX=43.75 CenterY=11.25 CenterZ=0 NormalX=0 NormalY=0 NormalZ=1 AngleXU=0 Radius=1.25
    g5: Circle CenterX=0.25 CenterY=11.25 CenterZ=0 NormalX=0 NormalY=0 NormalZ=1 AngleXU=0 Radius=1.25
    g6: Circle CenterX=0.25 CenterY=-11.25 CenterZ=0 NormalX=0 NormalY=0 NormalZ=1 AngleXU=0 Radius=1.25
    g7: Circle CenterX=43.75 CenterY=-11.25 CenterZ=0 NormalX=0 NormalY=0 NormalZ=1 AngleXU=0 Radius=1.25
  constraints (19):
    c: Coincident(g0,g1)
    c: Coincident(g1,g2)
    c: Coincident(g2,g3)
    c: Coincident(g3,g0)
    c: Horizontal(g0)
    c: Horizontal(g2)
    c: Vertical(g1)
    c: Symmetric(g0,g2,g-1)
    c: DistanceY(g3,g3) = 22.5
    c: DistanceX(g0,g0) = 43.5
    c: DistanceX(g-1,g2) = 0.25
    c: Coincident(g4,g0)
    c: Coincident(g5,g0)
    c: Coincident(g6,g2)
    c: Coincident(g7,g1)
    c: Equal(g5,g4)
    c: Equal(g4,g7)
    c: Equal(g7,g6)
    c: Diameter(g5) = 2.5
FEATURE [Sketcher::SketchObject] Sketch005
  AttachmentOffset = pos=(0,0,-3) rot=(0,0,1;0rad)
  FullyConstrained = true
  MapMode = 5
  Placement = pos=(-3,7e-16,-7e-16) rot=(0.57735,0.57735,0.57735;2.0944rad)
  Support = -> [YZ_Plane003]
  expr: .AttachmentOffset.Base.z = -Spreadsheet.BLDCWallThicknes
  expr: Constraints[10] = Spreadsheet.ConnectorPositionZ
  expr: Constraints[12] = Spreadsheet.ConnectorPocketDiameter
  expr: Constraints[7] = Spreadsheet.MountWidth
  sketch-geometry (5):
    g0: LineSegment StartX=-14 StartY=0 StartZ=0 EndX=-14 EndY=14 EndZ=0
    g1: ArcOfCircle CenterX=0 CenterY=14 CenterZ=0 NormalX=0 NormalY=0 NormalZ=1 AngleXU=0 Radius=14 StartAngle=1e-16 EndAngle=3.14159
    g2: LineSegment StartX=14 StartY=14 StartZ=0 EndX=14 EndY=0 EndZ=0
    g3: LineSegment StartX=14 StartY=0 StartZ=0 EndX=-14 EndY=0 EndZ=0
    g4: Circle CenterX=0 CenterY=14 CenterZ=0 NormalX=0 NormalY=0 NormalZ=1 AngleXU=0 Radius=11
  constraints (13):
    c: Vertical(g0)
    c: Tangent(g0,g1) = 1.5708
    c: Tangent(g1,g2) = 1.5708
    c: Coincident(g2,g3)
    c: Coincident(g3,g0)
    c: Horizontal(g3)
    c: PointOnObject(g1,g-2)
    c: DistanceX(g3,g3) = 28
    c: Vertical(g2)
    c: PointOnObject(g-1,g3)
    c: DistanceY(g2,g2) = 14
    c: Coincident(g4,g1)
    c: Diameter(g4) = 22
FEATURE [PartDesign::Pad] Pad001  label="Body"
  Direction = (1,-2e-16,3e-16)
  Length = 49
  Length2 = 10
  Placement = pos=(0,0,0) rot=(0.57735,0.57735,0.57735;2.0944rad)
  Profile = -> Sketch005
  ReferenceAxis = -> Sketch005 [N_Axis]
  Type = 0
  expr: Length = Spreadsheet.MountLength
FEATURE [Sketcher::SketchObject] Sketch006
  AttachmentOffset = pos=(0,0,-3) rot=(0,0,1;0rad)
  FullyConstrained = true
  MapMode = 5
  Placement = pos=(-3,7e-16,-7e-16) rot=(0.57735,0.57735,0.57735;2.0944rad)
  Support = -> [YZ_Plane003]
  expr: .AttachmentOffset.Base.z = -Spreadsheet.BLDCWallThicknes
  expr: Constraints[1] = Spreadsheet.ConnectorPocketDiameter
  expr: Constraints[2] = Spreadsheet.ConnectorPositionZ
  sketch-geometry (1):
    g0: Circle CenterX=0 CenterY=14 CenterZ=0 NormalX=0 NormalY=0 NormalZ=1 AngleXU=0 Radius=11
  constraints (3):
    c: PointOnObject(g0,g-2)
    c: Diameter(g0) = 22
    c: DistanceY(g-1,g0) = 14
FEATURE [PartDesign::Pocket] Pocket002  label="ConnectorPocket"
  BaseFeature = -> Pad001
  Direction = (-1,2e-16,-3e-16)
  Length = 46
  Length2 = 5
  Placement = pos=(0,0,0) rot=(0.57735,0.57735,0.57735;2.0944rad)
  Profile = -> Sketch006
  ReferenceAxis = -> Sketch006 [N_Axis]
  Reversed = true
  Type = 0
  expr: Length = Spreadsheet.ConnectorPocketDepth
FEATURE [Sketcher::SketchObject] Sketch007
  FullyConstrained = true
  MapMode = 5
  Support = -> [XY_Plane003]
  expr: Constraints[10] = Spreadsheet.CablePocketLength
  expr: Constraints[7] = Spreadsheet.ConnectorPocketDiameter + 1
  expr: Constraints[9] = Spreadsheet.CablePocketPositionH
  sketch-geometry (4):
    g0: LineSegment StartX=8 StartY=11.5 StartZ=0 EndX=43 EndY=11.5 EndZ=0
    g1: LineSegment StartX=43 StartY=11.5 StartZ=0 EndX=43 EndY=-11.5 EndZ=0
    g2: LineSegment StartX=43 StartY=-11.5 StartZ=0 EndX=8 EndY=-11.5 EndZ=0
    g3: LineSegment StartX=8 StartY=-11.5 StartZ=0 EndX=8 EndY=11.5 EndZ=0
  constraints (11):
    c: Coincident(g0,g1)
    c: Coincident(g1,g2)
    c: Coincident(g2,g3)
    c: Coincident(g3,g0)
    c: Horizontal(g0)
    c: Horizontal(g2)
    c: Vertical(g1)
    c: DistanceY(g1,g1) = 23
    c: Symmetric(g2,g0,g-1)
    c: DistanceX(g-1,g0) = 8
    c: DistanceX(g0,g0) = 35
FEATURE [PartDesign::Pocket] Pocket003  label="CablePocket001"
  BaseFeature = -> Pocket002
  Direction = (0,0,-1)
  Length = 14
  Length2 = 5
  Placement = pos=(0,0,0) rot=(0.57735,0.57735,0.57735;2.0944rad)
  Profile = -> Sketch007
  ReferenceAxis = -> Sketch007 [N_Axis]
  Reversed = true
  Type = 0
  expr: Length = Spreadsheet.ConnectorPositionZ
FEATURE [PartDesign::SubShapeBinder] Binder001  label="PositionHoleBinder"
  BindCopyOnChange = 0
  BindMode = 0
  ClaimChildren = false
  Context = -> Part [Body001.Binder001.]
  Fuse = false
  MakeFace = true
  OffsetFill = false
  OffsetIntersection = false
  OffsetJoinType = 0
  OffsetOpenResult = false
  PartialLoad = false
  Placement = pos=(0,0,-0.1) rot=(0,0,1;0rad)
  Relative = true
  Support = -> [Body[Hole.Sketch004.]]
  _Version = 2
FEATURE [PartDesign::Pocket] Pocket004
  BaseFeature = -> Pocket003
  Direction = (0,0,-1)
  Length = 3.1
  Length2 = 5
  Placement = pos=(0,0,0) rot=(0.57735,0.57735,0.57735;2.0944rad)
  Profile = -> Binder001
  Reversed = true
  Type = 0
  expr: Length = Spreadsheet.PositionHolePocketDepth
FEATURE [Sketcher::SketchObject] Sketch008
  FullyConstrained = true
  MapMode = 5
  Support = -> [XY_Plane005]
  expr: Constraints[2] = Spreadsheet.ConnectorPocketDiameter - 0.05
  expr: Constraints[3] = Spreadsheet.ConnectorThreadDiameter
  sketch-geometry (2):
    g0: Circle CenterX=0 CenterY=0 CenterZ=0 NormalX=0 NormalY=0 NormalZ=1 AngleXU=0 Radius=10.975
    g1: Circle CenterX=0 CenterY=0 CenterZ=0 NormalX=0 NormalY=0 NormalZ=1 AngleXU=0 Radius=9.015
  constraints (4):
    c: Coincident(g0,g-1)
    c: Coincident(g1,g0)
    c: Diameter(g0) = 21.95
    c: Diameter(g1) = 18.03
FEATURE [PartDesign::Pad] Pad002
  Direction = (0,0,1)
  Length = 11
  Length2 = 10
  Profile = -> Sketch008
  ReferenceAxis = -> Sketch008 [N_Axis]
  Type = 0
  expr: Length = Spreadsheet.ConnectorThreadLength
FEATURE [PartDesign::Body] Body002
  Group = -> [Sketch008,Pad002]
  Origin = -> Origin005
  Tip = -> Pad002
FEATURE [App::Part] Part002  label="ConnectorSocket"
  Group = -> [Body002]
  Origin = -> Origin004
  Placement = pos=(-18,0,47) rot=(0,1,0;1.5708rad)
FEATURE [PartDesign::Fillet] Fillet
  Base = -> Pocket004 [Edge20,Edge19,Edge21,Edge3]
  BaseFeature = -> Pocket004
  Placement = pos=(0,0,0) rot=(0.57735,0.57735,0.57735;2.0944rad)
  Radius = 1
  SupportTransform = false
  UseAllEdges = false
  expr: Radius = Spreadsheet.FiletSize
FEATURE [PartDesign::Fillet] Fillet001
  Base = -> Fillet [Edge70]
  BaseFeature = -> Fillet
  Placement = pos=(0,0,0) rot=(0.57735,0.57735,0.57735;2.0944rad)
  Radius = 1
  SupportTransform = false
  UseAllEdges = false
FEATURE [PartDesign::Body] Body001  label="Housing"
  Group = -> [Sketch005,Pad001,Sketch006,Pocket002,Sketch007,Pocket003,Binder001,Pocket004,Fillet,Fillet001]
  Origin = -> Origin003
  Placement = pos=(0,0,33.41) rot=(0,0,1;0rad)
  Tip = -> Fillet001
  expr: .Placement.Base.z = Spreadsheet.BodyPositionV
FEATURE [PartDesign::Pocket] Pocket  label="HolePocket"
  BaseFeature = -> Pocket001
  Direction = (0,0,-1)
  Length = 3.1
  Length2 = 5
  Placement = pos=(0,0,0) rot=(1,0,0;1.5708rad)
  Profile = -> Sketch004
  ReferenceAxis = -> Sketch004 [N_Axis]
  Type = 0
  expr: Length = Spreadsheet.PositionHolePocketDepth
FEATURE [PartDesign::Pocket] Pocket005  label="SidePocket"
  BaseFeature = -> Pocket
  Direction = (0,0,-1)
  Length = 5
  Length2 = 5
  Placement = pos=(0,0,0) rot=(1,0,0;1.5708rad)
  Profile = -> Sketch001
  ReferenceAxis = -> Sketch001 [N_Axis]
  Type = 1
FEATURE [App::TextDocument] Text_document  label="Cable Wiring"
  Text = BLDC motor to GX-20-12 connector: 57BLR70-24-02	\nPin	Colour	Description\n1,2	Orange	U\n3,4	Green	V\n5,6	Brown	W\n\n7	Black	GND\n8	Yellow	HAL A\n9	White	HAL B\n10	Blue	HAL C\n11	RED	+5V\n12	nc	nc\n\nBLDC driver to GX20-12 connector: DBLS-01S	\nPin	Colour	Description	\n1,2	Orange	MA (U)\n3,4	Green	MB (V)\n5,6	Brown	MC (W)\n\n7	Black	GND\n8	Yellow	HAL A\n9	White	HAL B\n10	Blue	HAL C\n11	RED	+5V\n12	nc	nc	\n\nCable GX20	\nPin	Colour	Description	\n1	black	MA (U)\n2	Brown	MA (U)\n3	Red	MB (V)\n4	Orange	MB (V)\n5	Yellow	MC (W)\n6	Green	MC (W)\n\n7	Blue	GND\n8	Violet	HAL A\n9	Grey	HAL B\n10	White	HAL C\n11	RED/Blue	+5V\n12	Grey/red	nc	\n	
FEATURE [Sketcher::SketchObject] Sketch009
  FullyConstrained = true
  MapMode = 5
  Support = -> [XY_Plane001]
  expr: Constraints[1] = Spreadsheet.ConnectorOuterDiameter
  expr: Constraints[2] = Spreadsheet.ConnectorBasePocketPositionH
  sketch-geometry (1):
    g0: Circle CenterX=22 CenterY=0 CenterZ=0 NormalX=0 NormalY=0 NormalZ=1 AngleXU=0 Radius=11
  constraints (3):
    c: PointOnObject(g0,g-1)
    c: Diameter(g0) = 22
    c: DistanceX(g-1,g0) = 22
FEATURE [PartDesign::Pocket] Pocket006  label="ConnectorPocket001"
  BaseFeature = -> Pocket005
  Direction = (0,0,-1)
  Length = 5
  Length2 = 5
  Placement = pos=(0,0,0) rot=(1,0,0;1.5708rad)
  Profile = -> Sketch009
  ReferenceAxis = -> Sketch009 [N_Axis]
  Reversed = true
  Type = 1
FEATURE [PartDesign::Body] Body  label="Base"
  Group = -> [Sketch,Revolution,Pad,Pocket001,Pocket,Pocket005,Sketch001,Sketch002,Sketch003,Sketch004,Sketch009,Pocket006]
  Origin = -> Origin001
  Tip = -> Pocket006
FEATURE [PartDesign::SubShapeBinder] Binder  label="PositionHoleBinder001"
  BindCopyOnChange = 0
  BindMode = 0
  ClaimChildren = false
  Context = -> Part [Body003.Binder.]
  Fuse = false
  MakeFace = true
  OffsetFill = false
  OffsetIntersection = false
  OffsetJoinType = 0
  OffsetOpenResult = false
  PartialLoad = false
  Relative = true
  Support = -> [Body[Pocket.Edge33]]
  _Version = 2
FEATURE [PartDesign::Pad] Pad003
  Direction = (0,0,1)
  Length = 5.2
  Length2 = 10
  Midplane = true
  Profile = -> Binder
  Type = 0
  expr: Length = Spreadsheet.PositionHolePocketDepth * 2 - 1
FEATURE [PartDesign::Chamfer] Chamfer
  Angle = 45
  Base = -> Pad003 [Face3,Face2]
  BaseFeature = -> Pad003
  ChamferType = 0
  FlipDirection = false
  Size = 0.5
  Size2 = 1
  SupportTransform = false
  UseAllEdges = false
FEATURE [PartDesign::Body] Body003  label="Positioner"
  Group = -> [Binder,Pad003,Chamfer]
  Origin = -> Origin007
  Tip = -> Chamfer
FEATURE [PartDesign::CoordinateSystem] Back
  AttacherType = Attacher::AttachEngine3D
  MapMode = 45
  Placement = pos=(46,1.3e-15,26.2879) rot=(0.707107,0,0.707107;3.14159rad)
  Support = -> [Pocket006]
FEATURE [PartDesign::CoordinateSystem] Front
  AttacherType = Attacher::AttachEngine3D
  MapMode = 45
  Placement = pos=(0,-2.6e-14,26.2687) rot=(0.707107,0,0.707107;3.14159rad)
  Support = -> [Pocket006]
FEATURE [App::Part] Part  label="ConnectorHousing"
  Group = -> [Body,Body001,Body003,Back,Front]
  Origin = -> Origin
---- part ToolPost.FCStd = doc fcstd_9a275cc0d884 ----
FCSTD DOCUMENT  (FreeCAD 0.21R31155 (Git))
Label: ToolPost
License: All rights reserved
LicenseURL: http://en.wikipedia.org/wiki/All_rights_reserved
objects: Sketcher::SketchObject×5, PartDesign::Pad×5, PartDesign::Body×2, PartDesign::CoordinateSystem×2, Spreadsheet::Sheet×1, App::Part×1
note: 19 computed .brp shape members not serialized (recipe doc carries the construction recipe); baked Part::Feature solids carry a one-line shape summary decoded from their .brp

FEATURE [Spreadsheet::Sheet] Spreadsheet
  Configuration = 0
  cells = A4=Part; B4=BaseWidth; C4=BaseLength; D4=BaseHeight; E4=ToolPostWidth; F4=ToolPostLength; G4=ToolPostThickness; H4=ToolBlockWidth; I4=ToolBlockLength; J4=ToolBlockThicknes; K4=TopThickness; A5==hiddenref(.Configuration.String); B5(BaseWidth)==.B6; C5(BaseLength)==.C6; D5(BaseHeight)==.D6; E5(ToolPostWidth)==.E6; F5(ToolPostLength)==.F6; G5(ToolPostThickness)==.G6; H5(ToolBlockWidth)==.H6; I5(ToolBlockLength)==.I6; J5(ToolBlockThicknes)==.J6; K5(TopThickness)==.K6; A6=BF290 QCTP; B6=80; C6=180; D6=26; E6=80; F6=80; G6=12.75; H6=64; I6=65; J6=24; K6=14; A12=CalculatedFields; A13=Test; B13(Test)==BaseWidth + BaseLength
  expr: .Configuration.Enum = cells[<<A6:|>>]
  expr: .cells.Bind.B5.ZZ5 = tuple(.cells; <<B>> + str(hiddenref(Configuration) + 6); <<ZZ>> + str(hiddenref(Configuration) + 6))
FEATURE [Sketcher::SketchObject] Sketch
  FullyConstrained = true
  MapMode = 5
  Support = -> [XY_Plane001]
  expr: Constraints[8] = Spreadsheet.BaseWidth
  expr: Constraints[9] = Spreadsheet.BaseLength
  sketch-geometry (4):
    g0: LineSegment StartX=0 StartY=-40 StartZ=0 EndX=180 EndY=-40 EndZ=0
    g1: LineSegment StartX=180 StartY=-40 StartZ=0 EndX=180 EndY=40 EndZ=0
    g2: LineSegment StartX=180 StartY=40 StartZ=0 EndX=0 EndY=40 EndZ=0
    g3: LineSegment StartX=0 StartY=40 StartZ=0 EndX=0 EndY=-40 EndZ=0
  constraints (11):
    c: Coincident(g0,g1)
    c: Coincident(g1,g2)
    c: Coincident(g2,g3)
    c: Coincident(g3,g0)
    c: Horizontal(g0)
    c: Horizontal(g2)
    c: Vertical(g1)
    c: Vertical(g3)
    c: DistanceY(g3,g3) = 80
    c: DistanceX(g2,g2) = 180
    c: Symmetric(g2,g0,g-1)
FEATURE [PartDesign::Pad] Pad
  Direction = (0,0,1)
  Length = 26
  Length2 = 10
  Profile = -> Sketch
  ReferenceAxis = -> Sketch [N_Axis]
  Type = 0
  expr: Length = Spreadsheet.BaseHeight
FEATURE [PartDesign::Body] Body  label="Base"
  Group = -> [Sketch,Pad]
  Origin = -> Origin001
  Tip = -> Pad
FEATURE [Sketcher::SketchObject] Sketch001
  AttachmentOffset = pos=(0,0,26) rot=(0,0,1;0rad)
  FullyConstrained = true
  MapMode = 5
  Placement = pos=(0,0,26) rot=(0,0,1;0rad)
  Support = -> [XY_Plane002]
  expr: .AttachmentOffset.Base.z = Spreadsheet.BaseHeight
  expr: Constraints[8] = Spreadsheet.ToolPostLength
  expr: Constraints[9] = Spreadsheet.ToolPostWidth
  sketch-geometry (4):
    g0: LineSegment StartX=0 StartY=40 StartZ=0 EndX=80 EndY=40 EndZ=0
    g1: LineSegment StartX=80 StartY=40 StartZ=0 EndX=80 EndY=-40 EndZ=0
    g2: LineSegment StartX=80 StartY=-40 StartZ=0 EndX=0 EndY=-40 EndZ=0
    g3: LineSegment StartX=0 StartY=-40 StartZ=0 EndX=0 EndY=40 EndZ=0
  constraints (11):
    c: Coincident(g0,g1)
    c: Coincident(g1,g2)
    c: Coincident(g2,g3)
    c: Coincident(g3,g0)
    c: Horizontal(g0)
    c: Horizontal(g2)
    c: Vertical(g1)
    c: Vertical(g3)
    c: DistanceX(g0,g0) = 80
    c: DistanceY(g3,g3) = 80
    c: Symmetric(g2,g0,g-1)
FEATURE [PartDesign::Pad] Pad001  label="ToolPost001"
  Direction = (0,0,1)
  Length = 12.75
  Length2 = 10
  Profile = -> Sketch001
  ReferenceAxis = -> Sketch001 [N_Axis]
  Type = 0
  expr: Length = Spreadsheet.ToolPostThickness
FEATURE [Sketcher::SketchObject] Sketch002
  FullyConstrained = true
  MapMode = 5
  Placement = pos=(0,0,38.75) rot=(0,0,1;0rad)
  Support = -> [Pad001]
  expr: Constraints[10] = Spreadsheet.ToolPostWidth / 2
  expr: Constraints[11] = Spreadsheet.ToolPostLength
  expr: Constraints[8] = Spreadsheet.ToolBlockLength
  expr: Constraints[9] = Spreadsheet.ToolBlockWidth
  sketch-geometry (4):
    g0: LineSegment StartX=15 StartY=24 StartZ=0 EndX=80 EndY=24 EndZ=0
    g1: LineSegment StartX=80 StartY=24 StartZ=0 EndX=80 EndY=-40 EndZ=0
    g2: LineSegment StartX=80 StartY=-40 StartZ=0 EndX=15 EndY=-40 EndZ=0
    g3: LineSegment StartX=15 StartY=-40 StartZ=0 EndX=15 EndY=24 EndZ=0
  constraints (12):
    c: Coincident(g0,g1)
    c: Coincident(g1,g2)
    c: Coincident(g2,g3)
    c: Coincident(g3,g0)
    c: Horizontal(g0)
    c: Horizontal(g2)
    c: Vertical(g1)
    c: Vertical(g3)
    c: DistanceX(g2,g2) = 65
    c: DistanceY(g1,g1) = 64
    c: DistanceY(g2,g-1) = 40
    c: DistanceX(g-1,g1) = 80
FEATURE [PartDesign::Pad] Pad002  label="ToolBlock"
  BaseFeature = -> Pad001
  Direction = (0,0,1)
  Length = 24
  Length2 = 10
  Profile = -> Sketch002
  ReferenceAxis = -> Sketch002 [N_Axis]
  Type = 0
  expr: Length = Spreadsheet.ToolBlockThicknes
FEATURE [Sketcher::SketchObject] Sketch003
  FullyConstrained = true
  MapMode = 5
  Placement = pos=(0,0,62.75) rot=(0,0,1;0rad)
  Support = -> [Pad002]
  expr: Constraints[8] = Spreadsheet.ToolPostWidth
  expr: Constraints[9] = Spreadsheet.ToolPostLength
  sketch-geometry (4):
    g0: LineSegment StartX=0 StartY=40 StartZ=0 EndX=80 EndY=40 EndZ=0
    g1: LineSegment StartX=80 StartY=40 StartZ=0 EndX=80 EndY=-40 EndZ=0
    g2: LineSegment StartX=80 StartY=-40 StartZ=0 EndX=0 EndY=-40 EndZ=0
    g3: LineSegment StartX=0 StartY=-40 StartZ=0 EndX=0 EndY=40 EndZ=0
  constraints (11):
    c: Coincident(g0,g1)
    c: Coincident(g1,g2)
    c: Coincident(g2,g3)
    c: Coincident(g3,g0)
    c: Horizontal(g0)
    c: Horizontal(g2)
    c: Vertical(g1)
    c: Vertical(g3)
    c: DistanceY(g3,g3) = 80
    c: DistanceX(g0,g0) = 80
    c: Symmetric(g2,g0,g-1)
FEATURE [PartDesign::Pad] Pad003  label="Top"
  BaseFeature = -> Pad002
  Direction = (0,0,1)
  Length = 14
  Length2 = 10
  Profile = -> Sketch003
  ReferenceAxis = -> Sketch003 [N_Axis]
  Type = 0
  expr: Length = Spreadsheet.TopThickness
FEATURE [PartDesign::CoordinateSystem] ToolBackRight
  AttacherType = Attacher::AttachEngine3D
  MapMode = 14
  Placement = pos=(80,24,38.75) rot=(1,0,0;1.5708rad)
  Support = -> [Pad003]
FEATURE [PartDesign::CoordinateSystem] ToolLeftBack
  AttacherType = Attacher::AttachEngine3D
  MapMode = 1
  Placement = pos=(15,-40,38.75) rot=(0,0,1;0rad)
  Support = -> [Pad003]
FEATURE [Sketcher::SketchObject] Sketch004
  FullyConstrained = true
  MapMode = 5
  Placement = pos=(0,0,76.75) rot=(0,0,1;0rad)
  Support = -> [Pad003]
  expr: Constraints[2] = Spreadsheet.ToolPostLength / 2
  sketch-geometry (1):
    g0: Circle CenterX=40 CenterY=0 CenterZ=0 NormalX=0 NormalY=0 NormalZ=1 AngleXU=0 Radius=10
  constraints (3):
    c: PointOnObject(g0,g-1)
    c: Diameter(g0) = 20
    c: DistanceX(g-1,g0) = 40
FEATURE [PartDesign::Pad] Pad004
  BaseFeature = -> Pad003
  Direction = (0,0,1)
  Length = 10
  Length2 = 10
  Profile = -> Sketch004
  ReferenceAxis = -> Sketch004 [N_Axis]
  Type = 0
FEATURE [PartDesign::Body] Body001  label="ToolHolder"
  Group = -> [Sketch001,Pad001,Sketch002,Pad002,Sketch003,Pad003,Sketch004,Pad004]
  Origin = -> Origin002
  Tip = -> Pad004
FEATURE [App::Part] Part  label="TopSlide"
  Group = -> [Body,Body001,ToolBackRight,ToolLeftBack]
  Origin = -> Origin
